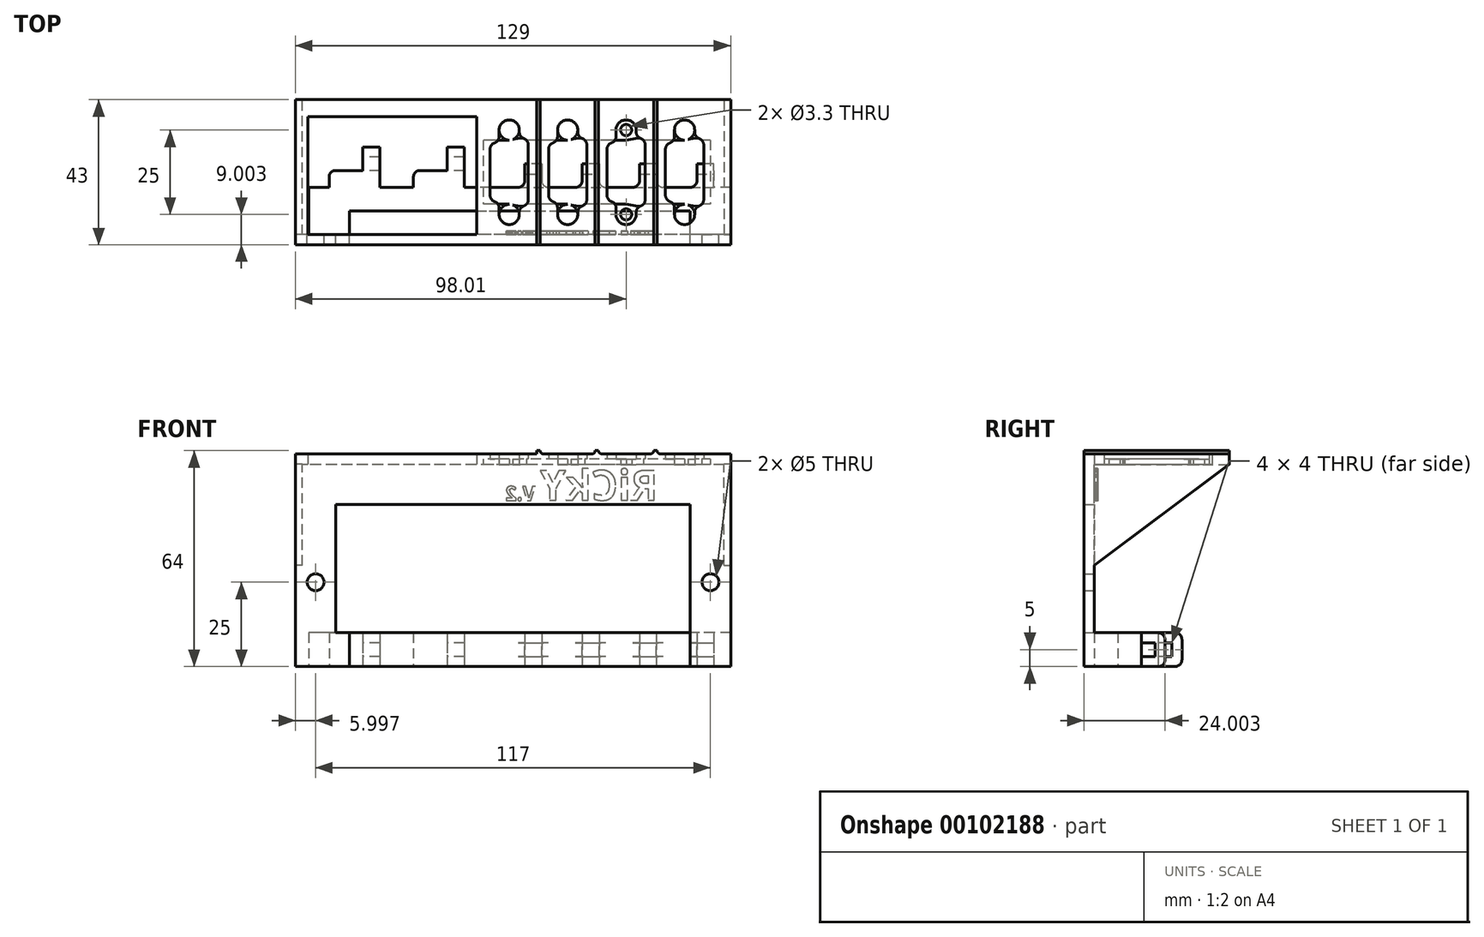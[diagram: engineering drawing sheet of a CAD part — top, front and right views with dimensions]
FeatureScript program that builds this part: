
annotation { "Feature Type Name" : "Feature", "Feature Type Description" : "" }
export const myFeature = defineFeature(function(context is Context, id is Id, definition is map)
    precondition{}
    {
        {
            var Q0;
            Q0=qCreatedBy(makeId("Top.planeOp"),FACE);
            var sketch = newSketch(context, id + "F0", { "sketchPlane" : qUnion([Q0])});
            skLineSegment(sketch, "E0", {"start": v(-4.26, 15.16) * mm, "end": v(16.74, 15.16) * mm});
            skLineSegment(sketch, "E1", {"start": v(-2.26, 3.83) * mm, "end": v(14.74, 3.83) * mm});
            skLineSegment(sketch, "E2", {"start": v(14.74, 3.83) * mm, "end": v(16.74, 15.16) * mm});
            skLineSegment(sketch, "E3", {"start": v(-2.26, 3.83) * mm, "end": v(-4.26, 15.16) * mm});
            skPoint(sketch, "E4", {"position": v(-3.26, 9.5) * mm});
            skPoint(sketch, "E5", {"position": v(15.74, 9.5) * mm});
            skPoint(sketch, "E6", {"position": v(-6.26, 9.5) * mm});
            skPoint(sketch, "E7", {"position": v(18.74, 9.5) * mm});
            skCircle(sketch, "E8", {"center": v(-6.26, 9.5) * mm, "radius": 3 * mm});
            skCircle(sketch, "E9", {"center": v(18.74, 9.5) * mm, "radius": 3 * mm});
            skLineSegment(sketch, "E10", {"start": v(-4.26, -2.17) * mm, "end": v(16.74, -2.17) * mm});
            skLineSegment(sketch, "E11", {"start": v(-2.26, -13.5) * mm, "end": v(14.74, -13.5) * mm});
            skLineSegment(sketch, "E12", {"start": v(14.74, -13.5) * mm, "end": v(16.74, -2.17) * mm});
            skLineSegment(sketch, "E13", {"start": v(-2.26, -13.5) * mm, "end": v(-4.26, -2.17) * mm});
            skPoint(sketch, "E14", {"position": v(-3.26, -7.83) * mm});
            skPoint(sketch, "E15", {"position": v(15.74, -7.83) * mm});
            skPoint(sketch, "E16", {"position": v(-6.26, -7.83) * mm});
            skPoint(sketch, "E17", {"position": v(18.74, -7.83) * mm});
            skCircle(sketch, "E18", {"center": v(-6.26, -7.83) * mm, "radius": 3 * mm});
            skCircle(sketch, "E19", {"center": v(18.74, -7.83) * mm, "radius": 3 * mm});
            skLineSegment(sketch, "E20", {"start": v(-4.26, 32.48) * mm, "end": v(16.74, 32.48) * mm});
            skLineSegment(sketch, "E21", {"start": v(-2.26, 21.16) * mm, "end": v(14.74, 21.16) * mm});
            skLineSegment(sketch, "E22", {"start": v(14.74, 21.16) * mm, "end": v(16.74, 32.48) * mm});
            skLineSegment(sketch, "E23", {"start": v(-2.26, 21.16) * mm, "end": v(-4.26, 32.48) * mm});
            skPoint(sketch, "E24", {"position": v(-3.26, 26.82) * mm});
            skPoint(sketch, "E25", {"position": v(15.74, 26.82) * mm});
            skPoint(sketch, "E26", {"position": v(-6.26, 26.82) * mm});
            skPoint(sketch, "E27", {"position": v(18.74, 26.82) * mm});
            skCircle(sketch, "E28", {"center": v(-6.26, 26.82) * mm, "radius": 3 * mm});
            skCircle(sketch, "E29", {"center": v(18.74, 26.82) * mm, "radius": 3 * mm});
            skLineSegment(sketch, "E30.bottom", {"start": v(27.74, 40.48) * mm, "end": v(-15.26, 40.48) * mm});
            skLineSegment(sketch, "E30.top", {"start": v(27.74, -88.52) * mm, "end": v(-15.26, -88.52) * mm});
            skLineSegment(sketch, "E30.left", {"start": v(27.74, 40.48) * mm, "end": v(27.74, -88.52) * mm});
            skLineSegment(sketch, "E30.right", {"start": v(-15.26, 40.48) * mm, "end": v(-15.26, -88.52) * mm});
            skLineSegment(sketch, "E31", {"start": v(-4.26, -19.5) * mm, "end": v(16.74, -19.5) * mm});
            skLineSegment(sketch, "E32", {"start": v(-2.26, -30.82) * mm, "end": v(14.74, -30.82) * mm});
            skLineSegment(sketch, "E33", {"start": v(14.74, -30.82) * mm, "end": v(16.74, -19.5) * mm});
            skLineSegment(sketch, "E34", {"start": v(-2.26, -30.82) * mm, "end": v(-4.26, -19.5) * mm});
            skPoint(sketch, "E35", {"position": v(-3.26, -25.15) * mm});
            skPoint(sketch, "E36", {"position": v(15.74, -25.15) * mm});
            skPoint(sketch, "E37", {"position": v(-6.26, -25.15) * mm});
            skPoint(sketch, "E38", {"position": v(18.74, -25.15) * mm});
            skCircle(sketch, "E39", {"center": v(-6.26, -25.15) * mm, "radius": 3 * mm});
            skCircle(sketch, "E40", {"center": v(18.74, -25.15) * mm, "radius": 3 * mm});
            skLineSegment(sketch, "E41", {"start": v(-6.26, 12.5) * mm, "end": v(-3.8, 12.5) * mm});
            skLineSegment(sketch, "E42", {"start": v(-6.26, 6.5) * mm, "end": v(-2.73, 6.5) * mm});
            skLineSegment(sketch, "E43", {"start": v(18.74, 12.5) * mm, "end": v(16.27, 12.5) * mm});
            skLineSegment(sketch, "E44", {"start": v(18.74, 6.5) * mm, "end": v(15.2, 6.5) * mm});
            skLineSegment(sketch, "E45", {"start": v(18.74, 29.82) * mm, "end": v(16.27, 29.82) * mm});
            skLineSegment(sketch, "E46", {"start": v(18.74, 23.82) * mm, "end": v(15.2, 23.82) * mm});
            skLineSegment(sketch, "E47", {"start": v(-6.26, 29.82) * mm, "end": v(-3.8, 29.82) * mm});
            skLineSegment(sketch, "E48", {"start": v(-6.26, 23.82) * mm, "end": v(-2.73, 23.82) * mm});
            skLineSegment(sketch, "E49", {"start": v(-6.26, -4.83) * mm, "end": v(-3.8, -4.83) * mm});
            skLineSegment(sketch, "E50", {"start": v(-6.26, -10.83) * mm, "end": v(-2.73, -10.83) * mm});
            skLineSegment(sketch, "E51", {"start": v(18.74, -10.83) * mm, "end": v(15.2, -10.83) * mm});
            skLineSegment(sketch, "E52", {"start": v(18.74, -4.83) * mm, "end": v(16.27, -4.83) * mm});
            skLineSegment(sketch, "E53", {"start": v(18.74, -22.15) * mm, "end": v(16.27, -22.15) * mm});
            skLineSegment(sketch, "E54", {"start": v(18.74, -28.15) * mm, "end": v(15.2, -28.15) * mm});
            skLineSegment(sketch, "E55", {"start": v(-6.26, -22.15) * mm, "end": v(-3.8, -22.15) * mm});
            skLineSegment(sketch, "E56", {"start": v(-6.26, -28.15) * mm, "end": v(-2.73, -28.15) * mm});
            skSolve(sketch);
        }
        {
            var Q0;
            Q0=makeQuery(id+"F0.imprint","IMPRINT",FACE,{"disambiguationData":[TD([[makeQuery(id+"F0.imprint","IMPRINT",EDGE,{"derivedFrom":sQuery(id+"F0.wireOp",EDGE,"E0")}),1.0]])]});
            extrude(context, id + "F1", {"entities" : qUnion([Q0]), "depth" : 3 * mm});
        }
        {
            var Q0;
            Q0=makeQuery(id+"F1.opExtrude","SWEPT_EDGE",EDGE,{"disambiguationData":[OSD([sQuery(id+"F0.wireOp",EDGE,"E0"),sQuery(id+"F0.wireOp",EDGE,"E3")])]});
            var Q1;
            Q1=makeQuery(id+"F1.opExtrude","SWEPT_EDGE",EDGE,{"disambiguationData":[OSD([sQuery(id+"F0.wireOp",EDGE,"E1"),sQuery(id+"F0.wireOp",EDGE,"E2")])]});
            var Q2;
            Q2=makeQuery(id+"F1.opExtrude","SWEPT_EDGE",EDGE,{"disambiguationData":[OSD([sQuery(id+"F0.wireOp",EDGE,"E0"),sQuery(id+"F0.wireOp",EDGE,"E2")])]});
            var Q3;
            Q3=makeQuery(id+"F1.opExtrude","SWEPT_EDGE",EDGE,{"disambiguationData":[OSD([sQuery(id+"F0.wireOp",EDGE,"E1"),sQuery(id+"F0.wireOp",EDGE,"E3")])]});
            var Q4;
            Q4=makeQuery(id+"F1.opExtrude","SWEPT_EDGE",EDGE,{"disambiguationData":[OSD([sQuery(id+"F0.wireOp",EDGE,"E20"),sQuery(id+"F0.wireOp",EDGE,"E23")])]});
            var Q5;
            Q5=makeQuery(id+"F1.opExtrude","SWEPT_EDGE",EDGE,{"disambiguationData":[OSD([sQuery(id+"F0.wireOp",EDGE,"E20"),sQuery(id+"F0.wireOp",EDGE,"E22")])]});
            var Q6;
            Q6=makeQuery(id+"F1.opExtrude","SWEPT_EDGE",EDGE,{"disambiguationData":[OSD([sQuery(id+"F0.wireOp",EDGE,"E21"),sQuery(id+"F0.wireOp",EDGE,"E23")])]});
            var Q7;
            Q7=makeQuery(id+"F1.opExtrude","SWEPT_EDGE",EDGE,{"disambiguationData":[OSD([sQuery(id+"F0.wireOp",EDGE,"E21"),sQuery(id+"F0.wireOp",EDGE,"E22")])]});
            var Q8;
            Q8=makeQuery(id+"F1.opExtrude","SWEPT_EDGE",EDGE,{"disambiguationData":[OSD([sQuery(id+"F0.wireOp",EDGE,"E11"),sQuery(id+"F0.wireOp",EDGE,"E12")])]});
            var Q9;
            Q9=makeQuery(id+"F1.opExtrude","SWEPT_EDGE",EDGE,{"disambiguationData":[OSD([sQuery(id+"F0.wireOp",EDGE,"E31"),sQuery(id+"F0.wireOp",EDGE,"E33")])]});
            var Q10;
            Q10=makeQuery(id+"F1.opExtrude","SWEPT_EDGE",EDGE,{"disambiguationData":[OSD([sQuery(id+"F0.wireOp",EDGE,"E10"),sQuery(id+"F0.wireOp",EDGE,"E12")])]});
            var Q11;
            Q11=makeQuery(id+"F1.opExtrude","SWEPT_EDGE",EDGE,{"disambiguationData":[OSD([sQuery(id+"F0.wireOp",EDGE,"E10"),sQuery(id+"F0.wireOp",EDGE,"E13")])]});
            var Q12;
            Q12=makeQuery(id+"F1.opExtrude","SWEPT_EDGE",EDGE,{"disambiguationData":[OSD([sQuery(id+"F0.wireOp",EDGE,"E31"),sQuery(id+"F0.wireOp",EDGE,"E34")])]});
            var Q13;
            Q13=makeQuery(id+"F1.opExtrude","SWEPT_EDGE",EDGE,{"disambiguationData":[OSD([sQuery(id+"F0.wireOp",EDGE,"E11"),sQuery(id+"F0.wireOp",EDGE,"E13")])]});
            var Q14;
            Q14=makeQuery(id+"F1.opExtrude","SWEPT_EDGE",EDGE,{"disambiguationData":[OSD([sQuery(id+"F0.wireOp",EDGE,"E32"),sQuery(id+"F0.wireOp",EDGE,"E34")])]});
            var Q15;
            Q15=makeQuery(id+"F1.opExtrude","SWEPT_EDGE",EDGE,{"disambiguationData":[OSD([sQuery(id+"F0.wireOp",EDGE,"E32"),sQuery(id+"F0.wireOp",EDGE,"E33")])]});
            fillet(context, id + "F2", {"entities" : qUnion([Q0, Q1, Q2, Q3, Q4, Q5, Q6, Q7, Q8, Q9, Q10, Q11, Q12, Q13, Q14, Q15]), "radius" : 2 * mm, "tangentPropagation" : true, "allowEdgeOverflow" : false});
        }
        {
            var Q0;
            Q0=makeQuery(id+"F0.imprint","IMPRINT",FACE,{"disambiguationData":[TD([[makeQuery(id+"F0.imprint","IMPRINT",EDGE,{"derivedFrom":sQuery(id+"F0.wireOp",EDGE,"E8")}),1.0]])]});
            var Q1;
            Q1=makeQuery(id+"F0.imprint","IMPRINT",FACE,{"disambiguationData":[TD([[makeQuery(id+"F0.imprint","IMPRINT",EDGE,{"derivedFrom":sQuery(id+"F0.wireOp",EDGE,"E9")}),1.0]])]});
            var Q2;
            {var subQ0=sQuery(id+"F0.wireOp",EDGE,"E28");var subQ1=sQuery(id+"F0.wireOp",EDGE,"E23");var subQ2=makeQuery(id+"F0.imprint","INTERSECT",VERTEX,{"disambiguationData":[OD(0.0)],"derivedFrom":[subQ1,subQ0]});Q2=makeQuery(id+"F0.imprint","IMPRINT",FACE,{"disambiguationData":[TD([[makeQuery(id+"F0.imprint","IMPRINT",EDGE,{"disambiguationData":[TD([[subQ2,-1.0]])],"derivedFrom":subQ1}),1.0]])]});}
            var Q3;
            {var subQ0=sQuery(id+"F0.wireOp",EDGE,"E29");var subQ1=sQuery(id+"F0.wireOp",EDGE,"E22");var subQ2=makeQuery(id+"F0.imprint","INTERSECT",VERTEX,{"disambiguationData":[OD(0.0)],"derivedFrom":[subQ1,subQ0]});Q3=makeQuery(id+"F0.imprint","IMPRINT",FACE,{"disambiguationData":[TD([[makeQuery(id+"F0.imprint","IMPRINT",EDGE,{"disambiguationData":[TD([[subQ2,-1.0]])],"derivedFrom":subQ1}),-1.0]])]});}
            var Q4;
            {var subQ0=sQuery(id+"F0.wireOp",EDGE,"E19");var subQ1=sQuery(id+"F0.wireOp",EDGE,"E12");var subQ2=makeQuery(id+"F0.imprint","INTERSECT",VERTEX,{"disambiguationData":[OD(0.0)],"derivedFrom":[subQ1,subQ0]});Q4=makeQuery(id+"F0.imprint","IMPRINT",FACE,{"disambiguationData":[TD([[makeQuery(id+"F0.imprint","IMPRINT",EDGE,{"disambiguationData":[TD([[subQ2,-1.0]])],"derivedFrom":subQ1}),-1.0]])]});}
            var Q5;
            {var subQ0=sQuery(id+"F0.wireOp",EDGE,"E18");var subQ1=sQuery(id+"F0.wireOp",EDGE,"E13");var subQ2=makeQuery(id+"F0.imprint","INTERSECT",VERTEX,{"disambiguationData":[OD(0.0)],"derivedFrom":[subQ1,subQ0]});Q5=makeQuery(id+"F0.imprint","IMPRINT",FACE,{"disambiguationData":[TD([[makeQuery(id+"F0.imprint","IMPRINT",EDGE,{"disambiguationData":[TD([[subQ2,-1.0]])],"derivedFrom":subQ1}),1.0]])]});}
            var Q6;
            {var subQ0=sQuery(id+"F0.wireOp",EDGE,"E40");var subQ1=sQuery(id+"F0.wireOp",EDGE,"E33");var subQ2=makeQuery(id+"F0.imprint","INTERSECT",VERTEX,{"disambiguationData":[OD(0.0)],"derivedFrom":[subQ1,subQ0]});Q6=makeQuery(id+"F0.imprint","IMPRINT",FACE,{"disambiguationData":[TD([[makeQuery(id+"F0.imprint","IMPRINT",EDGE,{"disambiguationData":[TD([[subQ2,-1.0]])],"derivedFrom":subQ1}),-1.0]])]});}
            var Q7;
            {var subQ0=sQuery(id+"F0.wireOp",EDGE,"E39");var subQ1=sQuery(id+"F0.wireOp",EDGE,"E34");var subQ2=makeQuery(id+"F0.imprint","INTERSECT",VERTEX,{"disambiguationData":[OD(0.0)],"derivedFrom":[subQ1,subQ0]});Q7=makeQuery(id+"F0.imprint","IMPRINT",FACE,{"disambiguationData":[TD([[makeQuery(id+"F0.imprint","IMPRINT",EDGE,{"disambiguationData":[TD([[subQ2,-1.0]])],"derivedFrom":subQ1}),1.0]])]});}
            var Q8;
            {var subQ0=sQuery(id+"F0.wireOp",EDGE,"E56");Q8=makeQuery(id+"F0.imprint","IMPRINT",FACE,{"disambiguationData":[TD([[makeQuery(id+"F0.imprint","IMPRINT",EDGE,{"derivedFrom":subQ0}),1.0]])]});}
            var Q9;
            {var subQ0=sQuery(id+"F0.wireOp",EDGE,"E55");Q9=makeQuery(id+"F0.imprint","IMPRINT",FACE,{"disambiguationData":[TD([[makeQuery(id+"F0.imprint","IMPRINT",EDGE,{"derivedFrom":subQ0}),-1.0]])]});}
            var Q10;
            {var subQ0=sQuery(id+"F0.wireOp",EDGE,"E54");Q10=makeQuery(id+"F0.imprint","IMPRINT",FACE,{"disambiguationData":[TD([[makeQuery(id+"F0.imprint","IMPRINT",EDGE,{"derivedFrom":subQ0}),-1.0]])]});}
            var Q11;
            {var subQ0=sQuery(id+"F0.wireOp",EDGE,"E53");Q11=makeQuery(id+"F0.imprint","IMPRINT",FACE,{"disambiguationData":[TD([[makeQuery(id+"F0.imprint","IMPRINT",EDGE,{"derivedFrom":subQ0}),1.0]])]});}
            var Q12;
            {var subQ0=sQuery(id+"F0.wireOp",EDGE,"E51");Q12=makeQuery(id+"F0.imprint","IMPRINT",FACE,{"disambiguationData":[TD([[makeQuery(id+"F0.imprint","IMPRINT",EDGE,{"derivedFrom":subQ0}),-1.0]])]});}
            var Q13;
            {var subQ0=sQuery(id+"F0.wireOp",EDGE,"E52");Q13=makeQuery(id+"F0.imprint","IMPRINT",FACE,{"disambiguationData":[TD([[makeQuery(id+"F0.imprint","IMPRINT",EDGE,{"derivedFrom":subQ0}),1.0]])]});}
            var Q14;
            {var subQ0=sQuery(id+"F0.wireOp",EDGE,"E50");Q14=makeQuery(id+"F0.imprint","IMPRINT",FACE,{"disambiguationData":[TD([[makeQuery(id+"F0.imprint","IMPRINT",EDGE,{"derivedFrom":subQ0}),1.0]])]});}
            var Q15;
            {var subQ0=sQuery(id+"F0.wireOp",EDGE,"E49");Q15=makeQuery(id+"F0.imprint","IMPRINT",FACE,{"disambiguationData":[TD([[makeQuery(id+"F0.imprint","IMPRINT",EDGE,{"derivedFrom":subQ0}),-1.0]])]});}
            var Q16;
            {var subQ0=sQuery(id+"F0.wireOp",EDGE,"E42");Q16=makeQuery(id+"F0.imprint","IMPRINT",FACE,{"disambiguationData":[TD([[makeQuery(id+"F0.imprint","IMPRINT",EDGE,{"derivedFrom":subQ0}),1.0]])]});}
            var Q17;
            {var subQ0=sQuery(id+"F0.wireOp",EDGE,"E41");Q17=makeQuery(id+"F0.imprint","IMPRINT",FACE,{"disambiguationData":[TD([[makeQuery(id+"F0.imprint","IMPRINT",EDGE,{"derivedFrom":subQ0}),-1.0]])]});}
            var Q18;
            {var subQ0=sQuery(id+"F0.wireOp",EDGE,"E44");Q18=makeQuery(id+"F0.imprint","IMPRINT",FACE,{"disambiguationData":[TD([[makeQuery(id+"F0.imprint","IMPRINT",EDGE,{"derivedFrom":subQ0}),-1.0]])]});}
            var Q19;
            {var subQ0=sQuery(id+"F0.wireOp",EDGE,"E43");Q19=makeQuery(id+"F0.imprint","IMPRINT",FACE,{"disambiguationData":[TD([[makeQuery(id+"F0.imprint","IMPRINT",EDGE,{"derivedFrom":subQ0}),1.0]])]});}
            var Q20;
            {var subQ0=sQuery(id+"F0.wireOp",EDGE,"E46");Q20=makeQuery(id+"F0.imprint","IMPRINT",FACE,{"disambiguationData":[TD([[makeQuery(id+"F0.imprint","IMPRINT",EDGE,{"derivedFrom":subQ0}),-1.0]])]});}
            var Q21;
            {var subQ0=sQuery(id+"F0.wireOp",EDGE,"E45");Q21=makeQuery(id+"F0.imprint","IMPRINT",FACE,{"disambiguationData":[TD([[makeQuery(id+"F0.imprint","IMPRINT",EDGE,{"derivedFrom":subQ0}),1.0]])]});}
            var Q22;
            {var subQ0=sQuery(id+"F0.wireOp",EDGE,"E47");Q22=makeQuery(id+"F0.imprint","IMPRINT",FACE,{"disambiguationData":[TD([[makeQuery(id+"F0.imprint","IMPRINT",EDGE,{"derivedFrom":subQ0}),-1.0]])]});}
            var Q23;
            {var subQ0=sQuery(id+"F0.wireOp",EDGE,"E48");Q23=makeQuery(id+"F0.imprint","IMPRINT",FACE,{"disambiguationData":[TD([[makeQuery(id+"F0.imprint","IMPRINT",EDGE,{"derivedFrom":subQ0}),1.0]])]});}
            extrude(context, id + "F3", {"entities" : qUnion([Q0, Q1, Q2, Q3, Q4, Q5, Q6, Q7, Q8, Q9, Q10, Q11, Q12, Q13, Q14, Q15, Q16, Q17, Q18, Q19, Q20, Q21, Q22, Q23]), "operationType" : NewBodyOperationType.ADD, "depth" : 1.5 * mm});
        }
        {
            var Q0;
            Q0=sQuery(id+"F0.wireOp",VERTEX,"E6");
            var Q1;
            Q1=sQuery(id+"F0.wireOp",VERTEX,"E7");
            var Q2;
            Q2=sQuery(id+"F0.wireOp",VERTEX,"E26");
            var Q3;
            Q3=sQuery(id+"F0.wireOp",VERTEX,"E27");
            var Q4;
            Q4=sQuery(id+"F0.wireOp",VERTEX,"E17");
            var Q5;
            Q5=sQuery(id+"F0.wireOp",VERTEX,"E16");
            var Q6;
            Q6=sQuery(id+"F0.wireOp",VERTEX,"E38");
            var Q7;
            Q7=sQuery(id+"F0.wireOp",VERTEX,"E37");
            var Q8;
            Q8=makeQuery(id+"F1.opExtrude","SWEPT_BODY",BODY,{"disambiguationData":[OSD([sQuery(id+"F0.wireOp",EDGE,"E0"),sQuery(id+"F0.wireOp",EDGE,"E1"),sQuery(id+"F0.wireOp",EDGE,"E2"),sQuery(id+"F0.wireOp",EDGE,"E3"),sQuery(id+"F0.wireOp",EDGE,"Wovf68Om-m2Ft-W6fg-vgO9-NATX11qrs2Ft.bottom"),sQuery(id+"F0.wireOp",EDGE,"Wovf68Om-m2Ft-W6fg-vgO9-NATX11qrs2Ft.top"),sQuery(id+"F0.wireOp",EDGE,"Wovf68Om-m2Ft-W6fg-vgO9-NATX11qrs2Ft.left"),sQuery(id+"F0.wireOp",EDGE,"Wovf68Om-m2Ft-W6fg-vgO9-NATX11qrs2Ft.right")])]});
            hole(context, id + "F4", {"style" : HoleStyle.SIMPLE, "endStyle" : HoleEndStyle.THROUGH, "oppositeDirection" : true, "holeDiameter" : 3.3 * mm, "startFromSketch" : true, "locations" : qUnion([Q0, Q1, Q2, Q3, Q4, Q5, Q6, Q7]), "scope" : qUnion([Q8]), "isTappedThrough" : true});
        }
        {
            var Q0;
            {var subQ0=sQuery(id+"F0.wireOp",EDGE,"E39");var subQ1=sQuery(id+"F0.wireOp",EDGE,"E34");var subQ2=sQuery(id+"F0.wireOp",EDGE,"E40");var subQ3=sQuery(id+"F0.wireOp",EDGE,"E33");var subQ4=sQuery(id+"F0.wireOp",EDGE,"E28");var subQ5=sQuery(id+"F0.wireOp",EDGE,"E23");var subQ6=sQuery(id+"F0.wireOp",EDGE,"E29");var subQ7=sQuery(id+"F0.wireOp",EDGE,"E22");var subQ8=sQuery(id+"F0.wireOp",EDGE,"E18");var subQ9=sQuery(id+"F0.wireOp",EDGE,"E13");var subQ10=sQuery(id+"F0.wireOp",EDGE,"E19");var subQ11=sQuery(id+"F0.wireOp",EDGE,"E12");var subQ12=sQuery(id+"F0.wireOp",EDGE,"E9");var subQ13=sQuery(id+"F0.wireOp",EDGE,"E8");Q0=makeQuery(id+"F3.boolean.opBoolean","MERGE",FACE,{"derivedFrom":[makeQuery(id+"F1.opExtrude","CAP_FACE",FACE,{"disambiguationData":[OSD([sQuery(id+"F0.wireOp",EDGE,"E0"),sQuery(id+"F0.wireOp",EDGE,"E1"),sQuery(id+"F0.wireOp",EDGE,"E2"),sQuery(id+"F0.wireOp",EDGE,"E3"),subQ13,subQ12,sQuery(id+"F0.wireOp",EDGE,"E10"),sQuery(id+"F0.wireOp",EDGE,"E11"),subQ11,subQ9,subQ8,subQ10,sQuery(id+"F0.wireOp",EDGE,"E20"),sQuery(id+"F0.wireOp",EDGE,"E21"),subQ7,subQ5,subQ4,subQ6,sQuery(id+"F0.wireOp",EDGE,"E30.bottom"),sQuery(id+"F0.wireOp",EDGE,"E30.top"),sQuery(id+"F0.wireOp",EDGE,"E30.left"),sQuery(id+"F0.wireOp",EDGE,"E30.right"),sQuery(id+"F0.wireOp",EDGE,"E31"),sQuery(id+"F0.wireOp",EDGE,"E32"),subQ3,subQ1,subQ0,subQ2])],"isStart":true}),makeQuery(id+"F3.opExtrude","CAP_FACE",FACE,{"disambiguationData":[OSD([subQ13])],"isStart":true}),makeQuery(id+"F3.opExtrude","CAP_FACE",FACE,{"disambiguationData":[OSD([subQ12])],"isStart":true}),makeQuery(id+"F3.opExtrude","CAP_FACE",FACE,{"disambiguationData":[OSD([subQ11,subQ10])],"isStart":true}),makeQuery(id+"F3.opExtrude","CAP_FACE",FACE,{"disambiguationData":[OSD([subQ9,subQ8])],"isStart":true}),makeQuery(id+"F3.opExtrude","CAP_FACE",FACE,{"disambiguationData":[OSD([subQ7,subQ6])],"isStart":true}),makeQuery(id+"F3.opExtrude","CAP_FACE",FACE,{"disambiguationData":[OSD([subQ5,subQ4])],"isStart":true}),makeQuery(id+"F3.opExtrude","CAP_FACE",FACE,{"disambiguationData":[OSD([subQ3,subQ2])],"isStart":true}),makeQuery(id+"F3.opExtrude","CAP_FACE",FACE,{"disambiguationData":[OSD([subQ1,subQ0])],"isStart":true})]});}
            var sketch = newSketch(context, id + "F5", { "sketchPlane" : qUnion([Q0])});
            skLineSegment(sketch, "E57.bottom", {"start": v(24.74, -40.48) * mm, "end": v(27.74, -40.48) * mm});
            skLineSegment(sketch, "E57.top", {"start": v(24.74, 88.52) * mm, "end": v(27.74, 88.52) * mm});
            skLineSegment(sketch, "E57.left", {"start": v(24.74, -40.48) * mm, "end": v(24.74, 88.52) * mm});
            skLineSegment(sketch, "E57.right", {"start": v(27.74, -40.48) * mm, "end": v(27.74, 88.52) * mm});
            skSolve(sketch);
        }
        {
            var Q0;
            Q0=makeQuery(id+"F5.imprint","IMPRINT",FACE,{"disambiguationData":[TD([[makeQuery(id+"F5.imprint","IMPRINT",EDGE,{"derivedFrom":sQuery(id+"F5.wireOp",EDGE,"E57.bottom")}),-1.0]])]});
            extrude(context, id + "F6", {"entities" : qUnion([Q0]), "operationType" : NewBodyOperationType.ADD, "depth" : 60 * mm});
        }
        {
            var Q0;
            Q0=makeQuery(id+"F6.boolean.opBoolean","MERGE",FACE,{"derivedFrom":[makeQuery(id+"F1.opExtrude","SWEPT_FACE",FACE,{"disambiguationData":[OSD([sQuery(id+"F0.wireOp",EDGE,"E30.bottom")])]}),makeQuery(id+"F6.opExtrude","SWEPT_FACE",FACE,{"disambiguationData":[OSD([sQuery(id+"F5.wireOp",EDGE,"E57.bottom")])]})]});
            var sketch = newSketch(context, id + "F7", { "sketchPlane" : qUnion([Q0])});
            skLineSegment(sketch, "E58", {"start": v(15.26, 0) * mm, "end": v(-24.74, -30) * mm});
            skLineSegment(sketch, "E59", {"start": v(-24.74, -30) * mm, "end": v(-24.74, 0) * mm});
            skLineSegment(sketch, "E60", {"start": v(-24.74, 0) * mm, "end": v(15.26, 0) * mm});
            skSolve(sketch);
        }
        {
            var Q0;
            Q0=makeQuery(id+"F6.boolean.opBoolean","MERGE",FACE,{"derivedFrom":[makeQuery(id+"F1.opExtrude","SWEPT_FACE",FACE,{"disambiguationData":[OSD([sQuery(id+"F0.wireOp",EDGE,"E30.top")])]}),makeQuery(id+"F6.opExtrude","SWEPT_FACE",FACE,{"disambiguationData":[OSD([sQuery(id+"F5.wireOp",EDGE,"E57.top")])]})]});
            var sketch = newSketch(context, id + "F8", { "sketchPlane" : qUnion([Q0])});
            skLineSegment(sketch, "E61", {"start": v(-15.26, 0) * mm, "end": v(24.74, -30) * mm});
            skSolve(sketch);
        }
        {
            var Q0;
            Q0=makeQuery(id+"F7.imprint","IMPRINT",FACE,{"disambiguationData":[TD([[makeQuery(id+"F7.imprint","IMPRINT",EDGE,{"derivedFrom":sQuery(id+"F7.wireOp",EDGE,"E58")}),-1.0]])]});
            extrude(context, id + "F9", {"entities" : qUnion([Q0]), "operationType" : NewBodyOperationType.ADD, "oppositeDirection" : true, "depth" : 2 * mm});
        }
        {
            var Q0;
            {var subQ0=sQuery(id+"F8.wireOp",EDGE,"E61");Q0=makeQuery(id+"F8.imprint","IMPRINT",FACE,{"disambiguationData":[TD([[makeQuery(id+"F8.imprint","IMPRINT",EDGE,{"derivedFrom":subQ0}),1.0]])]});}
            extrude(context, id + "F10", {"entities" : qUnion([Q0]), "operationType" : NewBodyOperationType.ADD, "oppositeDirection" : true, "depth" : 2 * mm});
        }
        {
            var Q0;
            Q0=makeQuery(id+"F6.opExtrude","SWEPT_FACE",FACE,{"disambiguationData":[OSD([sQuery(id+"F5.wireOp",EDGE,"E57.left")])]});
            var sketch = newSketch(context, id + "F11", { "sketchPlane" : qUnion([Q0])});
            skLineSegment(sketch, "E62.bottom", {"start": v(-28.48, -12) * mm, "end": v(76.52, -12) * mm});
            skLineSegment(sketch, "E62.top", {"start": v(-28.48, -52) * mm, "end": v(76.52, -52) * mm});
            skLineSegment(sketch, "E62.left", {"start": v(-28.48, -12) * mm, "end": v(-28.48, -52) * mm});
            skLineSegment(sketch, "E62.right", {"start": v(76.52, -12) * mm, "end": v(76.52, -52) * mm});
            skPoint(sketch, "E63.positionSnap0", {"position": v(24.02, 0) * mm});
            skSolve(sketch);
        }
        {
            var Q0;
            Q0=makeQuery(id+"F11.imprint","IMPRINT",FACE,{"disambiguationData":[TD([[makeQuery(id+"F11.imprint","IMPRINT",EDGE,{"derivedFrom":sQuery(id+"F11.wireOp",EDGE,"E62.bottom")}),-1.0]])]});
            extrude(context, id + "F12", {"entities" : qUnion([Q0]), "operationType" : NewBodyOperationType.REMOVE, "oppositeDirection" : true, "depth" : 3 * mm});
        }
        {
            var Q0;
            Q0=makeQuery(id+"F1.opExtrude","SWEPT_EDGE",EDGE,{"disambiguationData":[OSD([sQuery(id+"F0.wireOp",EDGE,"E34"),sQuery(id+"F0.wireOp",EDGE,"E56")])]});
            var Q1;
            Q1=makeQuery(id+"F1.opExtrude","SWEPT_EDGE",EDGE,{"disambiguationData":[OSD([sQuery(id+"F0.wireOp",EDGE,"E34"),sQuery(id+"F0.wireOp",EDGE,"E55")])]});
            var Q2;
            Q2=makeQuery(id+"F1.opExtrude","SWEPT_EDGE",EDGE,{"disambiguationData":[OSD([sQuery(id+"F0.wireOp",EDGE,"E33"),sQuery(id+"F0.wireOp",EDGE,"E54")])]});
            var Q3;
            Q3=makeQuery(id+"F1.opExtrude","SWEPT_EDGE",EDGE,{"disambiguationData":[OSD([sQuery(id+"F0.wireOp",EDGE,"E33"),sQuery(id+"F0.wireOp",EDGE,"E53")])]});
            var Q4;
            Q4=makeQuery(id+"F1.opExtrude","SWEPT_EDGE",EDGE,{"disambiguationData":[OSD([sQuery(id+"F0.wireOp",EDGE,"E12"),sQuery(id+"F0.wireOp",EDGE,"E52")])]});
            var Q5;
            Q5=makeQuery(id+"F1.opExtrude","SWEPT_EDGE",EDGE,{"disambiguationData":[OSD([sQuery(id+"F0.wireOp",EDGE,"E13"),sQuery(id+"F0.wireOp",EDGE,"E49")])]});
            var Q6;
            Q6=makeQuery(id+"F1.opExtrude","SWEPT_EDGE",EDGE,{"disambiguationData":[OSD([sQuery(id+"F0.wireOp",EDGE,"E13"),sQuery(id+"F0.wireOp",EDGE,"E50")])]});
            var Q7;
            Q7=makeQuery(id+"F1.opExtrude","SWEPT_EDGE",EDGE,{"disambiguationData":[OSD([sQuery(id+"F0.wireOp",EDGE,"E12"),sQuery(id+"F0.wireOp",EDGE,"E51")])]});
            var Q8;
            Q8=makeQuery(id+"F1.opExtrude","SWEPT_EDGE",EDGE,{"disambiguationData":[OSD([sQuery(id+"F0.wireOp",EDGE,"E3"),sQuery(id+"F0.wireOp",EDGE,"E42")])]});
            var Q9;
            Q9=makeQuery(id+"F1.opExtrude","SWEPT_EDGE",EDGE,{"disambiguationData":[OSD([sQuery(id+"F0.wireOp",EDGE,"E2"),sQuery(id+"F0.wireOp",EDGE,"E44")])]});
            var Q10;
            Q10=makeQuery(id+"F1.opExtrude","SWEPT_EDGE",EDGE,{"disambiguationData":[OSD([sQuery(id+"F0.wireOp",EDGE,"E22"),sQuery(id+"F0.wireOp",EDGE,"E46")])]});
            var Q11;
            Q11=makeQuery(id+"F1.opExtrude","SWEPT_EDGE",EDGE,{"disambiguationData":[OSD([sQuery(id+"F0.wireOp",EDGE,"E23"),sQuery(id+"F0.wireOp",EDGE,"E48")])]});
            var Q12;
            Q12=makeQuery(id+"F1.opExtrude","SWEPT_EDGE",EDGE,{"disambiguationData":[OSD([sQuery(id+"F0.wireOp",EDGE,"E3"),sQuery(id+"F0.wireOp",EDGE,"E41")])]});
            var Q13;
            Q13=makeQuery(id+"F1.opExtrude","SWEPT_EDGE",EDGE,{"disambiguationData":[OSD([sQuery(id+"F0.wireOp",EDGE,"E2"),sQuery(id+"F0.wireOp",EDGE,"E43")])]});
            var Q14;
            Q14=makeQuery(id+"F1.opExtrude","SWEPT_EDGE",EDGE,{"disambiguationData":[OSD([sQuery(id+"F0.wireOp",EDGE,"E22"),sQuery(id+"F0.wireOp",EDGE,"E45")])]});
            var Q15;
            Q15=makeQuery(id+"F1.opExtrude","SWEPT_EDGE",EDGE,{"disambiguationData":[OSD([sQuery(id+"F0.wireOp",EDGE,"E23"),sQuery(id+"F0.wireOp",EDGE,"E47")])]});
            fillet(context, id + "F13", {"entities" : qUnion([Q0, Q1, Q2, Q3, Q4, Q5, Q6, Q7, Q8, Q9, Q10, Q11, Q12, Q13, Q14, Q15]), "radius" : 2 * mm, "tangentPropagation" : true, "allowEdgeOverflow" : false});
        }
        {
            var Q0;
            Q0=makeQuery(id+"F1.opExtrude","SWEPT_BODY",BODY,{"disambiguationData":[OSD([sQuery(id+"F0.wireOp",EDGE,"E0"),sQuery(id+"F0.wireOp",EDGE,"E1"),sQuery(id+"F0.wireOp",EDGE,"E2"),sQuery(id+"F0.wireOp",EDGE,"E3"),sQuery(id+"F0.wireOp",EDGE,"E8"),sQuery(id+"F0.wireOp",EDGE,"E9"),sQuery(id+"F0.wireOp",EDGE,"E10"),sQuery(id+"F0.wireOp",EDGE,"E11"),sQuery(id+"F0.wireOp",EDGE,"E12"),sQuery(id+"F0.wireOp",EDGE,"E13"),sQuery(id+"F0.wireOp",EDGE,"E18"),sQuery(id+"F0.wireOp",EDGE,"E19"),sQuery(id+"F0.wireOp",EDGE,"E20"),sQuery(id+"F0.wireOp",EDGE,"E21"),sQuery(id+"F0.wireOp",EDGE,"E22"),sQuery(id+"F0.wireOp",EDGE,"E23"),sQuery(id+"F0.wireOp",EDGE,"E28"),sQuery(id+"F0.wireOp",EDGE,"E29"),sQuery(id+"F0.wireOp",EDGE,"E30.bottom"),sQuery(id+"F0.wireOp",EDGE,"E30.top"),sQuery(id+"F0.wireOp",EDGE,"E30.left"),sQuery(id+"F0.wireOp",EDGE,"E30.right"),sQuery(id+"F0.wireOp",EDGE,"E31"),sQuery(id+"F0.wireOp",EDGE,"E32"),sQuery(id+"F0.wireOp",EDGE,"E33"),sQuery(id+"F0.wireOp",EDGE,"E34"),sQuery(id+"F0.wireOp",EDGE,"E39"),sQuery(id+"F0.wireOp",EDGE,"E40"),sQuery(id+"F0.wireOp",EDGE,"E41"),sQuery(id+"F0.wireOp",EDGE,"E42"),sQuery(id+"F0.wireOp",EDGE,"E43"),sQuery(id+"F0.wireOp",EDGE,"E44"),sQuery(id+"F0.wireOp",EDGE,"E45"),sQuery(id+"F0.wireOp",EDGE,"E46"),sQuery(id+"F0.wireOp",EDGE,"E47"),sQuery(id+"F0.wireOp",EDGE,"E48"),sQuery(id+"F0.wireOp",EDGE,"E49"),sQuery(id+"F0.wireOp",EDGE,"E50"),sQuery(id+"F0.wireOp",EDGE,"E51"),sQuery(id+"F0.wireOp",EDGE,"E52"),sQuery(id+"F0.wireOp",EDGE,"E53"),sQuery(id+"F0.wireOp",EDGE,"E54"),sQuery(id+"F0.wireOp",EDGE,"E55"),sQuery(id+"F0.wireOp",EDGE,"E56")])]});
            var Q1;
            Q1=makeQuery(id+"F6.boolean.opBoolean","MERGE",EDGE,{"derivedFrom":[makeQuery(id+"F1.opExtrude","SWEPT_EDGE",EDGE,{"disambiguationData":[OSD([sQuery(id+"F0.wireOp",EDGE,"E30.top"),sQuery(id+"F0.wireOp",EDGE,"E30.left")])]}),makeQuery(id+"F6.opExtrude","SWEPT_EDGE",EDGE,{"disambiguationData":[OSD([sQuery(id+"F5.wireOp",EDGE,"E57.top"),sQuery(id+"F5.wireOp",EDGE,"E57.right")])]})]});
            transform(context, id + "F14", {"entities" : qUnion([Q0]), "transformType" : TransformType.ROTATION, "transformAxis" : qUnion([Q1]), "angle" : 90 * degree, "makeCopy" : false});
        }
        {
            var Q0;
            {var subQ0=sQuery(id+"F8EoDyI46MSBQYM_1.wireOp",EDGE,"hDJBzksL-QToe-umQY-51Cy-cnB0OUttW4tD.bottom");var subQ1=sQuery(id+"F8EoDyI46MSBQYM_1.wireOp",EDGE,"pdXBlQge-3E0r-zufv-tM46-rPFQcP1RDKDh.bottom");var subQ2=sQuery(id+"F0.wireOp",EDGE,"E56");var subQ3=sQuery(id+"F0.wireOp",EDGE,"E55");var subQ4=sQuery(id+"F0.wireOp",EDGE,"E39");var subQ5=sQuery(id+"F0.wireOp",EDGE,"E34");var subQ6=sQuery(id+"F0.wireOp",EDGE,"E54");var subQ7=sQuery(id+"F0.wireOp",EDGE,"E53");var subQ8=sQuery(id+"F0.wireOp",EDGE,"E40");var subQ9=sQuery(id+"F0.wireOp",EDGE,"E33");var subQ10=sQuery(id+"F0.wireOp",EDGE,"E48");var subQ11=sQuery(id+"F0.wireOp",EDGE,"E47");var subQ12=sQuery(id+"F0.wireOp",EDGE,"E28");var subQ13=sQuery(id+"F0.wireOp",EDGE,"E23");var subQ14=sQuery(id+"F0.wireOp",EDGE,"E46");var subQ15=sQuery(id+"F0.wireOp",EDGE,"E45");var subQ16=sQuery(id+"F0.wireOp",EDGE,"E29");var subQ17=sQuery(id+"F0.wireOp",EDGE,"E22");var subQ18=sQuery(id+"F0.wireOp",EDGE,"E50");var subQ19=sQuery(id+"F0.wireOp",EDGE,"E49");var subQ20=sQuery(id+"F0.wireOp",EDGE,"E18");var subQ21=sQuery(id+"F0.wireOp",EDGE,"E13");var subQ22=sQuery(id+"F0.wireOp",EDGE,"E52");var subQ23=sQuery(id+"F0.wireOp",EDGE,"E51");var subQ24=sQuery(id+"F0.wireOp",EDGE,"E19");var subQ25=sQuery(id+"F0.wireOp",EDGE,"E12");var subQ26=sQuery(id+"F0.wireOp",EDGE,"E42");var subQ27=sQuery(id+"F0.wireOp",EDGE,"E41");var subQ28=sQuery(id+"F0.wireOp",EDGE,"E8");var subQ29=sQuery(id+"F0.wireOp",EDGE,"E3");var subQ30=sQuery(id+"F0.wireOp",EDGE,"E44");var subQ31=sQuery(id+"F0.wireOp",EDGE,"E43");var subQ32=sQuery(id+"F0.wireOp",EDGE,"E9");var subQ33=sQuery(id+"F0.wireOp",EDGE,"E2");Q0=makeQuery(id+"FhEWOf1GAh2BQzi_1.boolean.opBoolean","MERGE",FACE,{"derivedFrom":[makeQuery(id+"FwzRGj0mSM9Jiqs_1.boolean.opBoolean","MERGE",FACE,{"derivedFrom":[makeQuery(id+"F3.boolean.opBoolean","MERGE",FACE,{"derivedFrom":[makeQuery(id+"F1.opExtrude","CAP_FACE",FACE,{"disambiguationData":[OSD([sQuery(id+"F0.wireOp",EDGE,"E0"),sQuery(id+"F0.wireOp",EDGE,"E1"),subQ33,subQ29,subQ28,subQ32,sQuery(id+"F0.wireOp",EDGE,"E10"),sQuery(id+"F0.wireOp",EDGE,"E11"),subQ25,subQ21,subQ20,subQ24,sQuery(id+"F0.wireOp",EDGE,"E20"),sQuery(id+"F0.wireOp",EDGE,"E21"),subQ17,subQ13,subQ12,subQ16,sQuery(id+"F0.wireOp",EDGE,"E30.bottom"),sQuery(id+"F0.wireOp",EDGE,"E30.top"),sQuery(id+"F0.wireOp",EDGE,"E30.left"),sQuery(id+"F0.wireOp",EDGE,"E30.right"),sQuery(id+"F0.wireOp",EDGE,"E31"),sQuery(id+"F0.wireOp",EDGE,"E32"),subQ9,subQ5,subQ4,subQ8,subQ27,subQ26,subQ31,subQ30,subQ15,subQ14,subQ11,subQ10,subQ19,subQ18,subQ23,subQ22,subQ7,subQ6,subQ3,subQ2])],"isStart":true}),makeQuery(id+"F3.opExtrude","CAP_FACE",FACE,{"disambiguationData":[OSD([subQ33,subQ32,subQ31,subQ30])],"isStart":true}),makeQuery(id+"F3.opExtrude","CAP_FACE",FACE,{"disambiguationData":[OSD([subQ29,subQ28,subQ27,subQ26])],"isStart":true}),makeQuery(id+"F3.opExtrude","CAP_FACE",FACE,{"disambiguationData":[OSD([subQ25,subQ24,subQ23,subQ22])],"isStart":true}),makeQuery(id+"F3.opExtrude","CAP_FACE",FACE,{"disambiguationData":[OSD([subQ21,subQ20,subQ19,subQ18])],"isStart":true}),makeQuery(id+"F3.opExtrude","CAP_FACE",FACE,{"disambiguationData":[OSD([subQ17,subQ16,subQ15,subQ14])],"isStart":true}),makeQuery(id+"F3.opExtrude","CAP_FACE",FACE,{"disambiguationData":[OSD([subQ13,subQ12,subQ11,subQ10])],"isStart":true}),makeQuery(id+"F3.opExtrude","CAP_FACE",FACE,{"disambiguationData":[OSD([subQ9,subQ8,subQ7,subQ6])],"isStart":true}),makeQuery(id+"F3.opExtrude","CAP_FACE",FACE,{"disambiguationData":[OSD([subQ5,subQ4,subQ3,subQ2])],"isStart":true})]}),makeQuery(id+"FwzRGj0mSM9Jiqs_1.opExtrude","SWEPT_FACE",FACE,{"disambiguationData":[OSD([subQ1])]}),makeQuery(id+"FwzRGj0mSM9Jiqs_1.opExtrude","SWEPT_FACE",FACE,{"disambiguationData":[OSD([subQ0])]})]}),makeQuery(id+"FhEWOf1GAh2BQzi_1.opExtrude","SWEPT_FACE",FACE,{"disambiguationData":[OSD([subQ1])]}),makeQuery(id+"FhEWOf1GAh2BQzi_1.opExtrude","SWEPT_FACE",FACE,{"disambiguationData":[OSD([subQ0])]})]});}
            var sketch = newSketch(context, id + "F15", { "sketchPlane" : qUnion([Q0])});
            skLineSegment(sketch, "E64.bottom", {"start": v(150.74, 57.52) * mm, "end": v(83.44, 57.52) * mm});
            skLineSegment(sketch, "E64.top", {"start": v(150.74, 76.52) * mm, "end": v(83.44, 76.52) * mm});
            skLineSegment(sketch, "E64.left", {"start": v(150.74, 57.52) * mm, "end": v(150.74, 76.52) * mm});
            skLineSegment(sketch, "E64.right", {"start": v(83.44, 57.52) * mm, "end": v(83.44, 76.52) * mm});
            skSolve(sketch);
        }
        {
            var Q0;
            {var subQ10=sQuery(id+"F0.wireOp",EDGE,"E0");var subQ24=makeQuery(id+"F1.opExtrude","CAP_EDGE",EDGE,{"disambiguationData":[OSD([subQ10])],"isStart":true});Q0=makeQuery(id+"F15.imprint","IMPRINT",FACE,{"disambiguationData":[TD([[makeQuery(id+"F15.imprint","IMPRINT",EDGE,{"derivedFrom":subQ24}),-1.0]])]});}
            var Q1;
            {var subQ0=sQuery(id+"F15.wireOp",EDGE,"E64.left");Q1=makeQuery(id+"F15.imprint","IMPRINT",FACE,{"disambiguationData":[TD([[makeQuery(id+"F15.imprint","IMPRINT",EDGE,{"derivedFrom":subQ0}),1.0]])]});}
            var Q2;
            {var subQ9=sQuery(id+"F0.wireOp",EDGE,"E1");Q2=makeQuery(id+"F15.imprint","IMPRINT",FACE,{"disambiguationData":[TD([[makeQuery(id+"F15.imprint","IMPRINT",EDGE,{"derivedFrom":makeQuery(id+"F1.opExtrude","CAP_EDGE",EDGE,{"disambiguationData":[OSD([subQ9])],"isStart":true})}),1.0]])]});}
            var Q3;
            {var subQ9=sQuery(id+"F0.wireOp",EDGE,"E11");Q3=makeQuery(id+"F15.imprint","IMPRINT",FACE,{"disambiguationData":[TD([[makeQuery(id+"F15.imprint","IMPRINT",EDGE,{"derivedFrom":makeQuery(id+"F1.opExtrude","CAP_EDGE",EDGE,{"disambiguationData":[OSD([subQ9])],"isStart":true})}),1.0]])]});}
            var Q4;
            {var subQ10=sQuery(id+"F15.wireOp",EDGE,"E64.right");Q4=makeQuery(id+"F15.imprint","IMPRINT",FACE,{"disambiguationData":[TD([[makeQuery(id+"F15.imprint","IMPRINT",EDGE,{"derivedFrom":subQ10}),-1.0]])]});}
            extrude(context, id + "F16", {"entities" : qUnion([Q0, Q1, Q2, Q3, Q4]), "operationType" : NewBodyOperationType.REMOVE, "oppositeDirection" : true, "depth" : 1.5 * mm});
        }
        {
            var Q0;
            {var subQ0=sQuery(id+"F0.wireOp",EDGE,"E56");var subQ1=sQuery(id+"F0.wireOp",EDGE,"E55");var subQ2=sQuery(id+"F0.wireOp",EDGE,"E39");var subQ3=sQuery(id+"F0.wireOp",EDGE,"E34");var subQ4=sQuery(id+"F0.wireOp",EDGE,"E54");var subQ5=sQuery(id+"F0.wireOp",EDGE,"E53");var subQ6=sQuery(id+"F0.wireOp",EDGE,"E40");var subQ7=sQuery(id+"F0.wireOp",EDGE,"E33");var subQ8=sQuery(id+"F0.wireOp",EDGE,"E48");var subQ9=sQuery(id+"F0.wireOp",EDGE,"E47");var subQ10=sQuery(id+"F0.wireOp",EDGE,"E28");var subQ11=sQuery(id+"F0.wireOp",EDGE,"E23");var subQ12=sQuery(id+"F0.wireOp",EDGE,"E46");var subQ13=sQuery(id+"F0.wireOp",EDGE,"E45");var subQ14=sQuery(id+"F0.wireOp",EDGE,"E29");var subQ15=sQuery(id+"F0.wireOp",EDGE,"E22");var subQ16=sQuery(id+"F0.wireOp",EDGE,"E50");var subQ17=sQuery(id+"F0.wireOp",EDGE,"E49");var subQ18=sQuery(id+"F0.wireOp",EDGE,"E18");var subQ19=sQuery(id+"F0.wireOp",EDGE,"E13");var subQ20=sQuery(id+"F0.wireOp",EDGE,"E52");var subQ21=sQuery(id+"F0.wireOp",EDGE,"E51");var subQ22=sQuery(id+"F0.wireOp",EDGE,"E19");var subQ23=sQuery(id+"F0.wireOp",EDGE,"E12");var subQ24=sQuery(id+"F0.wireOp",EDGE,"E42");var subQ25=sQuery(id+"F0.wireOp",EDGE,"E41");var subQ26=sQuery(id+"F0.wireOp",EDGE,"E8");var subQ27=sQuery(id+"F0.wireOp",EDGE,"E3");var subQ28=sQuery(id+"F0.wireOp",EDGE,"E44");var subQ29=sQuery(id+"F0.wireOp",EDGE,"E43");var subQ30=sQuery(id+"F0.wireOp",EDGE,"E9");var subQ31=sQuery(id+"F0.wireOp",EDGE,"E2");Q0=makeQuery(id+"F3.boolean.opBoolean","MERGE",FACE,{"derivedFrom":[makeQuery(id+"F1.opExtrude","CAP_FACE",FACE,{"disambiguationData":[OSD([sQuery(id+"F0.wireOp",EDGE,"E0"),sQuery(id+"F0.wireOp",EDGE,"E1"),subQ31,subQ27,subQ26,subQ30,sQuery(id+"F0.wireOp",EDGE,"E10"),sQuery(id+"F0.wireOp",EDGE,"E11"),subQ23,subQ19,subQ18,subQ22,sQuery(id+"F0.wireOp",EDGE,"E20"),sQuery(id+"F0.wireOp",EDGE,"E21"),subQ15,subQ11,subQ10,subQ14,sQuery(id+"F0.wireOp",EDGE,"E30.bottom"),sQuery(id+"F0.wireOp",EDGE,"E30.top"),sQuery(id+"F0.wireOp",EDGE,"E30.left"),sQuery(id+"F0.wireOp",EDGE,"E30.right"),sQuery(id+"F0.wireOp",EDGE,"E31"),sQuery(id+"F0.wireOp",EDGE,"E32"),subQ7,subQ3,subQ2,subQ6,subQ25,subQ24,subQ29,subQ28,subQ13,subQ12,subQ9,subQ8,subQ17,subQ16,subQ21,subQ20,subQ5,subQ4,subQ1,subQ0])],"isStart":true}),makeQuery(id+"F3.opExtrude","CAP_FACE",FACE,{"disambiguationData":[OSD([subQ31,subQ30,subQ29,subQ28])],"isStart":true}),makeQuery(id+"F3.opExtrude","CAP_FACE",FACE,{"disambiguationData":[OSD([subQ27,subQ26,subQ25,subQ24])],"isStart":true}),makeQuery(id+"F3.opExtrude","CAP_FACE",FACE,{"disambiguationData":[OSD([subQ23,subQ22,subQ21,subQ20])],"isStart":true}),makeQuery(id+"F3.opExtrude","CAP_FACE",FACE,{"disambiguationData":[OSD([subQ19,subQ18,subQ17,subQ16])],"isStart":true}),makeQuery(id+"F3.opExtrude","CAP_FACE",FACE,{"disambiguationData":[OSD([subQ15,subQ14,subQ13,subQ12])],"isStart":true}),makeQuery(id+"F3.opExtrude","CAP_FACE",FACE,{"disambiguationData":[OSD([subQ11,subQ10,subQ9,subQ8])],"isStart":true}),makeQuery(id+"F3.opExtrude","CAP_FACE",FACE,{"disambiguationData":[OSD([subQ7,subQ6,subQ5,subQ4])],"isStart":true}),makeQuery(id+"F3.opExtrude","CAP_FACE",FACE,{"disambiguationData":[OSD([subQ3,subQ2,subQ1,subQ0])],"isStart":true})]});}
            var sketch = newSketch(context, id + "F17", { "sketchPlane" : qUnion([Q0])});
            skLineSegment(sketch, "E65.bottom", {"start": v(81.44, 50.52) * mm, "end": v(31.44, 50.52) * mm});
            skLineSegment(sketch, "E65.top", {"start": v(81.44, 85.52) * mm, "end": v(31.44, 85.52) * mm});
            skLineSegment(sketch, "E65.left", {"start": v(81.44, 50.52) * mm, "end": v(81.44, 85.52) * mm});
            skLineSegment(sketch, "E65.right", {"start": v(31.44, 50.52) * mm, "end": v(31.44, 85.52) * mm});
            skSolve(sketch);
        }
        {
            var Q0;
            Q0=makeQuery(id+"F17.imprint","IMPRINT",FACE,{"disambiguationData":[TD([[makeQuery(id+"F17.imprint","IMPRINT",EDGE,{"derivedFrom":sQuery(id+"F17.wireOp",EDGE,"E65.bottom")}),-1.0]])]});
            extrude(context, id + "F18", {"entities" : qUnion([Q0]), "operationType" : NewBodyOperationType.REMOVE, "oppositeDirection" : true, "depth" : 3 * mm});
        }
        {
            var Q0;
            Q0=makeQuery(id+"F18.boolean.opBoolean","MERGE",FACE,{"derivedFrom":[makeQuery(id+"F6.opExtrude","SWEPT_FACE",FACE,{"disambiguationData":[OSD([sQuery(id+"F5.wireOp",EDGE,"E57.left")])]}),makeQuery(id+"F18.opExtrude","SWEPT_FACE",FACE,{"disambiguationData":[OSD([sQuery(id+"F17.wireOp",EDGE,"E65.top")])]})]});
            var sketch = newSketch(context, id + "F19", { "sketchPlane" : qUnion([Q0])});
            skPoint(sketch, "E66", {"position": v(-33.74, -35) * mm});
            skPoint(sketch, "E67", {"position": v(-150.74, -35) * mm});
            skSolve(sketch);
        }
        {
            var Q0;
            Q0=sQuery(id+"F19.wireOp",VERTEX,"E66");
            var Q1;
            Q1=sQuery(id+"F19.wireOp",VERTEX,"E67");
            var Q2;
            Q2=makeQuery(id+"F1.opExtrude","SWEPT_BODY",BODY,{"disambiguationData":[OSD([sQuery(id+"F0.wireOp",EDGE,"E0"),sQuery(id+"F0.wireOp",EDGE,"E1"),sQuery(id+"F0.wireOp",EDGE,"E2"),sQuery(id+"F0.wireOp",EDGE,"E3"),sQuery(id+"F0.wireOp",EDGE,"E8"),sQuery(id+"F0.wireOp",EDGE,"E9"),sQuery(id+"F0.wireOp",EDGE,"E10"),sQuery(id+"F0.wireOp",EDGE,"E11"),sQuery(id+"F0.wireOp",EDGE,"E12"),sQuery(id+"F0.wireOp",EDGE,"E13"),sQuery(id+"F0.wireOp",EDGE,"E18"),sQuery(id+"F0.wireOp",EDGE,"E19"),sQuery(id+"F0.wireOp",EDGE,"E20"),sQuery(id+"F0.wireOp",EDGE,"E21"),sQuery(id+"F0.wireOp",EDGE,"E22"),sQuery(id+"F0.wireOp",EDGE,"E23"),sQuery(id+"F0.wireOp",EDGE,"E28"),sQuery(id+"F0.wireOp",EDGE,"E29"),sQuery(id+"F0.wireOp",EDGE,"E30.bottom"),sQuery(id+"F0.wireOp",EDGE,"E30.top"),sQuery(id+"F0.wireOp",EDGE,"E30.left"),sQuery(id+"F0.wireOp",EDGE,"E30.right"),sQuery(id+"F0.wireOp",EDGE,"E31"),sQuery(id+"F0.wireOp",EDGE,"E32"),sQuery(id+"F0.wireOp",EDGE,"E33"),sQuery(id+"F0.wireOp",EDGE,"E34"),sQuery(id+"F0.wireOp",EDGE,"E39"),sQuery(id+"F0.wireOp",EDGE,"E40"),sQuery(id+"F0.wireOp",EDGE,"E41"),sQuery(id+"F0.wireOp",EDGE,"E42"),sQuery(id+"F0.wireOp",EDGE,"E43"),sQuery(id+"F0.wireOp",EDGE,"E44"),sQuery(id+"F0.wireOp",EDGE,"E45"),sQuery(id+"F0.wireOp",EDGE,"E46"),sQuery(id+"F0.wireOp",EDGE,"E47"),sQuery(id+"F0.wireOp",EDGE,"E48"),sQuery(id+"F0.wireOp",EDGE,"E49"),sQuery(id+"F0.wireOp",EDGE,"E50"),sQuery(id+"F0.wireOp",EDGE,"E51"),sQuery(id+"F0.wireOp",EDGE,"E52"),sQuery(id+"F0.wireOp",EDGE,"E53"),sQuery(id+"F0.wireOp",EDGE,"E54"),sQuery(id+"F0.wireOp",EDGE,"E55"),sQuery(id+"F0.wireOp",EDGE,"E56")])]});
            hole(context, id + "F20", {"style" : HoleStyle.SIMPLE, "endStyle" : HoleEndStyle.THROUGH, "holeDiameter" : 5 * mm, "locations" : qUnion([Q0, Q1]), "scope" : qUnion([Q2]), "isTappedThrough" : true});
        }
        {
            var Q0;
            Q0=makeQuery(id+"F18.boolean.opBoolean","MERGE",FACE,{"derivedFrom":[makeQuery(id+"F6.opExtrude","SWEPT_FACE",FACE,{"disambiguationData":[OSD([sQuery(id+"F5.wireOp",EDGE,"E57.left")])]}),makeQuery(id+"F18.opExtrude","SWEPT_FACE",FACE,{"disambiguationData":[OSD([sQuery(id+"F17.wireOp",EDGE,"E65.top")])]})]});
            var sketch = newSketch(context, id + "F21", { "sketchPlane" : qUnion([Q0])});
            skText(sketch, "E68", { "text": "RiCkY", "fontName": "OpenSans-Bold.ttf"});
            const initialGuessF21  = {"E68": [-0.1352, -0.01067, 1, 0, 0.00885]};
            skSetInitialGuess(sketch, initialGuessF21);
            skSolve(sketch);
        }
        {
            var Q0;
            Q0 = qSketchRegion(id + "F21", true);
            extrude(context, id + "F22", {"entities" : qUnion([Q0]), "operationType" : NewBodyOperationType.ADD, "depth" : 1 * mm});
        }
        {
            var Q0;
            Q0=makeQuery(id+"F12.boolean.opBoolean","COPY",FACE,{"derivedFrom":makeQuery(id+"F12.opExtrude","SWEPT_FACE",FACE,{"disambiguationData":[OSD([sQuery(id+"F11.wireOp",EDGE,"E62.top")])]})});
            extrude(context, id + "F23", {"entities" : qUnion([Q0]), "operationType" : NewBodyOperationType.ADD, "depth" : 2 * mm});
        }
        {
            var Q0;
            {var subQ0=sQuery(id+"F11.wireOp",EDGE,"E62.top");var subQ26=sQuery(id+"F0.wireOp",EDGE,"E30.bottom");var subQ46=sQuery(id+"F5.wireOp",EDGE,"E57.left");Q0=makeQuery(id+"F23.boolean.opBoolean","MERGE",FACE,{"derivedFrom":[makeQuery(id+"F22.boolean.opBoolean","SPLIT",FACE,{"disambiguationData":[TD([makeQuery(id+"F1.opExtrude","SWEPT_FACE",FACE,{"disambiguationData":[OSD([subQ26])]})])],"derivedFrom":makeQuery(id+"F18.boolean.opBoolean","MERGE",FACE,{"derivedFrom":[makeQuery(id+"F6.opExtrude","SWEPT_FACE",FACE,{"disambiguationData":[OSD([subQ46])]}),makeQuery(id+"F18.opExtrude","SWEPT_FACE",FACE,{"disambiguationData":[OSD([sQuery(id+"F17.wireOp",EDGE,"E65.top")])]})]})}),makeQuery(id+"F23.opExtrude","SWEPT_FACE",FACE,{"disambiguationData":[OSD([subQ0]),TDD([makeQuery(id+"F12.boolean.opBoolean","COPY",EDGE,{"derivedFrom":makeQuery(id+"F12.opExtrude","CAP_EDGE",EDGE,{"disambiguationData":[OSD([subQ0])],"isStart":true})})])]})]});}
            var sketch = newSketch(context, id + "F24", { "sketchPlane" : qUnion([Q0])});
            skLineSegment(sketch, "E69.bottom", {"start": v(-156.74, -50) * mm, "end": v(-31.74, -50) * mm});
            skLineSegment(sketch, "E69.top", {"start": v(-156.74, -60) * mm, "end": v(-31.74, -60) * mm});
            skLineSegment(sketch, "E69.left", {"start": v(-156.74, -50) * mm, "end": v(-156.74, -60) * mm});
            skLineSegment(sketch, "E69.right", {"start": v(-31.74, -50) * mm, "end": v(-31.74, -60) * mm});
            skSolve(sketch);
        }
        {
            var Q0;
            Q0=makeQuery(id+"F24.imprint","IMPRINT",FACE,{"disambiguationData":[TD([[makeQuery(id+"F24.imprint","IMPRINT",EDGE,{"derivedFrom":sQuery(id+"F24.wireOp",EDGE,"E69.top")}),1.0]])]});
            extrude(context, id + "F25", {"entities" : qUnion([Q0]), "operationType" : NewBodyOperationType.ADD, "depth" : 14 * mm});
        }
        {
            var Q0;
            Q0=makeQuery(id+"F25.opExtrude","CAP_FACE",FACE,{"disambiguationData":[OSD([sQuery(id+"F24.wireOp",EDGE,"E69.bottom"),sQuery(id+"F24.wireOp",EDGE,"E69.top"),sQuery(id+"F24.wireOp",EDGE,"E69.left"),sQuery(id+"F24.wireOp",EDGE,"E69.right")])],"isStart":false});
            var sketch = newSketch(context, id + "F26", { "sketchPlane" : qUnion([Q0])});
            skLineSegment(sketch, "E70.bottom", {"start": v(-151.74, -50) * mm, "end": v(-146.74, -50) * mm});
            skLineSegment(sketch, "E70.top", {"start": v(-151.74, -60) * mm, "end": v(-146.74, -60) * mm});
            skLineSegment(sketch, "E70.left", {"start": v(-151.74, -50) * mm, "end": v(-151.74, -60) * mm});
            skLineSegment(sketch, "E70.right", {"start": v(-146.74, -50) * mm, "end": v(-146.74, -60) * mm});
            skLineSegment(sketch, "E71.bottom", {"start": v(-134.74, -50) * mm, "end": v(-129.74, -50) * mm});
            skLineSegment(sketch, "E71.top", {"start": v(-134.74, -60) * mm, "end": v(-129.74, -60) * mm});
            skLineSegment(sketch, "E71.left", {"start": v(-134.74, -50) * mm, "end": v(-134.74, -60) * mm});
            skLineSegment(sketch, "E71.right", {"start": v(-129.74, -50) * mm, "end": v(-129.74, -60) * mm});
            skLineSegment(sketch, "E72.bottom", {"start": v(-117.74, -50) * mm, "end": v(-112.74, -50) * mm});
            skLineSegment(sketch, "E72.top", {"start": v(-117.74, -60) * mm, "end": v(-112.74, -60) * mm});
            skLineSegment(sketch, "E72.left", {"start": v(-117.74, -50) * mm, "end": v(-117.74, -60) * mm});
            skLineSegment(sketch, "E72.right", {"start": v(-112.74, -50) * mm, "end": v(-112.74, -60) * mm});
            skLineSegment(sketch, "E73.bottom", {"start": v(-100.74, -50) * mm, "end": v(-95.74, -50) * mm});
            skLineSegment(sketch, "E73.top", {"start": v(-100.74, -60) * mm, "end": v(-95.74, -60) * mm});
            skLineSegment(sketch, "E73.left", {"start": v(-100.74, -50) * mm, "end": v(-100.74, -60) * mm});
            skLineSegment(sketch, "E73.right", {"start": v(-95.74, -50) * mm, "end": v(-95.74, -60) * mm});
            skLineSegment(sketch, "E74.bottom", {"start": v(-77.74, -50) * mm, "end": v(-62.74, -50) * mm});
            skLineSegment(sketch, "E74.top", {"start": v(-77.74, -60) * mm, "end": v(-62.74, -60) * mm});
            skLineSegment(sketch, "E74.left", {"start": v(-77.74, -50) * mm, "end": v(-77.74, -60) * mm});
            skLineSegment(sketch, "E74.right", {"start": v(-62.74, -50) * mm, "end": v(-62.74, -60) * mm});
            skLineSegment(sketch, "E75.bottom", {"start": v(-52.74, -50) * mm, "end": v(-37.74, -50) * mm});
            skLineSegment(sketch, "E75.top", {"start": v(-52.74, -60) * mm, "end": v(-37.74, -60) * mm});
            skLineSegment(sketch, "E75.left", {"start": v(-52.74, -50) * mm, "end": v(-52.74, -60) * mm});
            skLineSegment(sketch, "E75.right", {"start": v(-37.74, -50) * mm, "end": v(-37.74, -60) * mm});
            skSolve(sketch);
        }
        {
            var Q0;
            Q0=makeQuery(id+"F26.imprint","IMPRINT",FACE,{"disambiguationData":[TD([[makeQuery(id+"F26.imprint","IMPRINT",EDGE,{"derivedFrom":sQuery(id+"F26.wireOp",EDGE,"E73.bottom")}),-1.0]])]});
            var Q1;
            Q1=makeQuery(id+"F26.imprint","IMPRINT",FACE,{"disambiguationData":[TD([[makeQuery(id+"F26.imprint","IMPRINT",EDGE,{"derivedFrom":sQuery(id+"F26.wireOp",EDGE,"E72.bottom")}),-1.0]])]});
            var Q2;
            Q2=makeQuery(id+"F26.imprint","IMPRINT",FACE,{"disambiguationData":[TD([[makeQuery(id+"F26.imprint","IMPRINT",EDGE,{"derivedFrom":sQuery(id+"F26.wireOp",EDGE,"E71.bottom")}),-1.0]])]});
            var Q3;
            Q3=makeQuery(id+"F26.imprint","IMPRINT",FACE,{"disambiguationData":[TD([[makeQuery(id+"F26.imprint","IMPRINT",EDGE,{"derivedFrom":sQuery(id+"F26.wireOp",EDGE,"E70.bottom")}),-1.0]])]});
            extrude(context, id + "F27", {"entities" : qUnion([Q0, Q1, Q2, Q3]), "operationType" : NewBodyOperationType.ADD, "depth" : 7 * mm});
        }
        {
            var Q0;
            Q0=makeQuery(id+"F26.imprint","IMPRINT",FACE,{"disambiguationData":[TD([[makeQuery(id+"F26.imprint","IMPRINT",EDGE,{"derivedFrom":sQuery(id+"F26.wireOp",EDGE,"E74.bottom")}),-1.0]])]});
            var Q1;
            Q1=makeQuery(id+"F26.imprint","IMPRINT",FACE,{"disambiguationData":[TD([[makeQuery(id+"F26.imprint","IMPRINT",EDGE,{"derivedFrom":sQuery(id+"F26.wireOp",EDGE,"E75.bottom")}),-1.0]])]});
            extrude(context, id + "F28", {"entities" : qUnion([Q0, Q1]), "operationType" : NewBodyOperationType.ADD, "depth" : 5 * mm});
        }
        {
            var Q0;
            Q0=makeQuery(id+"F28.opExtrude","CAP_FACE",FACE,{"disambiguationData":[OSD([sQuery(id+"F26.wireOp",EDGE,"E74.bottom"),sQuery(id+"F26.wireOp",EDGE,"E74.top"),sQuery(id+"F26.wireOp",EDGE,"E74.left"),sQuery(id+"F26.wireOp",EDGE,"E74.right")])],"isStart":false});
            var sketch = newSketch(context, id + "F29", { "sketchPlane" : qUnion([Q0])});
            skLineSegment(sketch, "E76.bottom", {"start": v(-77.74, -50) * mm, "end": v(-72.74, -50) * mm});
            skLineSegment(sketch, "E76.top", {"start": v(-77.74, -60) * mm, "end": v(-72.74, -60) * mm});
            skLineSegment(sketch, "E76.left", {"start": v(-77.74, -50) * mm, "end": v(-77.74, -60) * mm});
            skLineSegment(sketch, "E76.right", {"start": v(-72.74, -50) * mm, "end": v(-72.74, -60) * mm});
            skSolve(sketch);
        }
        {
            var Q0;
            Q0=makeQuery(id+"F28.opExtrude","CAP_FACE",FACE,{"disambiguationData":[OSD([sQuery(id+"F26.wireOp",EDGE,"E75.bottom"),sQuery(id+"F26.wireOp",EDGE,"E75.top"),sQuery(id+"F26.wireOp",EDGE,"E75.left"),sQuery(id+"F26.wireOp",EDGE,"E75.right")])],"isStart":false});
            var sketch = newSketch(context, id + "F30", { "sketchPlane" : qUnion([Q0])});
            skLineSegment(sketch, "E77.bottom", {"start": v(-52.74, -50) * mm, "end": v(-47.74, -50) * mm});
            skLineSegment(sketch, "E77.top", {"start": v(-52.74, -60) * mm, "end": v(-47.74, -60) * mm});
            skLineSegment(sketch, "E77.left", {"start": v(-52.74, -50) * mm, "end": v(-52.74, -60) * mm});
            skLineSegment(sketch, "E77.right", {"start": v(-47.74, -50) * mm, "end": v(-47.74, -60) * mm});
            skSolve(sketch);
        }
        {
            var Q0;
            Q0=makeQuery(id+"F30.imprint","IMPRINT",FACE,{"disambiguationData":[TD([[makeQuery(id+"F30.imprint","IMPRINT",EDGE,{"derivedFrom":sQuery(id+"F30.wireOp",EDGE,"E77.bottom")}),-1.0]])]});
            var Q1;
            Q1=makeQuery(id+"F29.imprint","IMPRINT",FACE,{"disambiguationData":[TD([[makeQuery(id+"F29.imprint","IMPRINT",EDGE,{"derivedFrom":sQuery(id+"F29.wireOp",EDGE,"E76.bottom")}),-1.0]])]});
            extrude(context, id + "F31", {"entities" : qUnion([Q0, Q1]), "operationType" : NewBodyOperationType.ADD, "depth" : 7 * mm});
        }
        {
            var Q0;
            Q0=makeQuery(id+"F27.opExtrude","SWEPT_FACE",FACE,{"disambiguationData":[OSD([sQuery(id+"F26.wireOp",EDGE,"E70.left")])]});
            var sketch = newSketch(context, id + "F32", { "sketchPlane" : qUnion([Q0])});
            skLineSegment(sketch, "E78.bottom", {"start": v(-71.52, -53) * mm, "end": v(-67.52, -53) * mm});
            skLineSegment(sketch, "E78.top", {"start": v(-71.52, -57) * mm, "end": v(-67.52, -57) * mm});
            skLineSegment(sketch, "E78.left", {"start": v(-71.52, -53) * mm, "end": v(-71.52, -57) * mm});
            skLineSegment(sketch, "E78.right", {"start": v(-67.52, -53) * mm, "end": v(-67.52, -57) * mm});
            skSolve(sketch);
        }
        {
            var Q0;
            Q0=makeQuery(id+"F32.imprint","IMPRINT",FACE,{"disambiguationData":[TD([[makeQuery(id+"F32.imprint","IMPRINT",EDGE,{"derivedFrom":sQuery(id+"F32.wireOp",EDGE,"E78.bottom")}),-1.0]])]});
            extrude(context, id + "F33", {"entities" : qUnion([Q0]), "operationType" : NewBodyOperationType.REMOVE, "oppositeDirection" : true, "depth" : 65 * mm});
        }
        {
            var Q0;
            Q0=makeQuery(id+"F27.opExtrude","CAP_EDGE",EDGE,{"disambiguationData":[OSD([sQuery(id+"F26.wireOp",EDGE,"E71.top")])],"isStart":false});
            var Q1;
            Q1=makeQuery(id+"F27.opExtrude","CAP_EDGE",EDGE,{"disambiguationData":[OSD([sQuery(id+"F26.wireOp",EDGE,"E71.bottom")])],"isStart":false});
            var Q2;
            Q2=makeQuery(id+"F27.opExtrude","CAP_EDGE",EDGE,{"disambiguationData":[OSD([sQuery(id+"F26.wireOp",EDGE,"E70.top")])],"isStart":false});
            var Q3;
            Q3=makeQuery(id+"F27.opExtrude","CAP_EDGE",EDGE,{"disambiguationData":[OSD([sQuery(id+"F26.wireOp",EDGE,"E70.bottom")])],"isStart":false});
            var Q4;
            Q4=makeQuery(id+"F27.opExtrude","CAP_EDGE",EDGE,{"disambiguationData":[OSD([sQuery(id+"F26.wireOp",EDGE,"E72.top")])],"isStart":false});
            var Q5;
            Q5=makeQuery(id+"F27.opExtrude","CAP_EDGE",EDGE,{"disambiguationData":[OSD([sQuery(id+"F26.wireOp",EDGE,"E72.bottom")])],"isStart":false});
            var Q6;
            Q6=makeQuery(id+"F27.opExtrude","CAP_EDGE",EDGE,{"disambiguationData":[OSD([sQuery(id+"F26.wireOp",EDGE,"E73.top")])],"isStart":false});
            var Q7;
            Q7=makeQuery(id+"F27.opExtrude","CAP_EDGE",EDGE,{"disambiguationData":[OSD([sQuery(id+"F26.wireOp",EDGE,"E73.bottom")])],"isStart":false});
            var Q8;
            {var subQ0=sQuery(id+"F26.wireOp",EDGE,"E73.left");var subQ1=sQuery(id+"F24.wireOp",EDGE,"E69.top");Q8=makeQuery(id+"F33.boolean.opBoolean","SPLIT",EDGE,{"disambiguationData":[TD([makeQuery(id+"F25.opExtrude","SWEPT_FACE",FACE,{"disambiguationData":[OSD([subQ1])]})])],"derivedFrom":makeQuery(id+"F27.opExtrude","CAP_EDGE",EDGE,{"disambiguationData":[OSD([subQ0])],"isStart":true})});}
            var Q9;
            {var subQ0=sQuery(id+"F26.wireOp",EDGE,"E73.left");Q9=makeQuery(id+"F33.boolean.opBoolean","SPLIT",EDGE,{"disambiguationData":[TD([makeQuery(id+"F23.opExtrude","CAP_FACE",FACE,{"disambiguationData":[OSD([sQuery(id+"F11.wireOp",EDGE,"E62.top")])],"isStart":false})])],"derivedFrom":makeQuery(id+"F27.opExtrude","CAP_EDGE",EDGE,{"disambiguationData":[OSD([subQ0])],"isStart":true})});}
            var Q10;
            {var subQ0=sQuery(id+"F26.wireOp",EDGE,"E72.left");var subQ1=sQuery(id+"F24.wireOp",EDGE,"E69.top");Q10=makeQuery(id+"F33.boolean.opBoolean","SPLIT",EDGE,{"disambiguationData":[TD([makeQuery(id+"F25.opExtrude","SWEPT_FACE",FACE,{"disambiguationData":[OSD([subQ1])]})])],"derivedFrom":makeQuery(id+"F27.opExtrude","CAP_EDGE",EDGE,{"disambiguationData":[OSD([subQ0])],"isStart":true})});}
            var Q11;
            {var subQ1=sQuery(id+"F26.wireOp",EDGE,"E72.left");Q11=makeQuery(id+"F33.boolean.opBoolean","SPLIT",EDGE,{"disambiguationData":[TD([makeQuery(id+"F23.opExtrude","CAP_FACE",FACE,{"disambiguationData":[OSD([sQuery(id+"F11.wireOp",EDGE,"E62.top")])],"isStart":false})])],"derivedFrom":makeQuery(id+"F27.opExtrude","CAP_EDGE",EDGE,{"disambiguationData":[OSD([subQ1])],"isStart":true})});}
            var Q12;
            {var subQ0=sQuery(id+"F24.wireOp",EDGE,"E69.top");var subQ1=sQuery(id+"F26.wireOp",EDGE,"E71.left");Q12=makeQuery(id+"F33.boolean.opBoolean","SPLIT",EDGE,{"disambiguationData":[TD([makeQuery(id+"F25.opExtrude","SWEPT_FACE",FACE,{"disambiguationData":[OSD([subQ0])]})])],"derivedFrom":makeQuery(id+"F27.opExtrude","CAP_EDGE",EDGE,{"disambiguationData":[OSD([subQ1])],"isStart":true})});}
            var Q13;
            {var subQ0=sQuery(id+"F26.wireOp",EDGE,"E71.left");Q13=makeQuery(id+"F33.boolean.opBoolean","SPLIT",EDGE,{"disambiguationData":[TD([makeQuery(id+"F23.opExtrude","CAP_FACE",FACE,{"disambiguationData":[OSD([sQuery(id+"F11.wireOp",EDGE,"E62.top")])],"isStart":false})])],"derivedFrom":makeQuery(id+"F27.opExtrude","CAP_EDGE",EDGE,{"disambiguationData":[OSD([subQ0])],"isStart":true})});}
            var Q14;
            {var subQ0=sQuery(id+"F26.wireOp",EDGE,"E70.left");var subQ1=sQuery(id+"F24.wireOp",EDGE,"E69.top");Q14=makeQuery(id+"F33.boolean.opBoolean","SPLIT",EDGE,{"disambiguationData":[TD([makeQuery(id+"F25.opExtrude","SWEPT_FACE",FACE,{"disambiguationData":[OSD([subQ1])]})])],"derivedFrom":makeQuery(id+"F27.opExtrude","CAP_EDGE",EDGE,{"disambiguationData":[OSD([subQ0])],"isStart":true})});}
            var Q15;
            {var subQ0=sQuery(id+"F26.wireOp",EDGE,"E70.left");Q15=makeQuery(id+"F33.boolean.opBoolean","SPLIT",EDGE,{"disambiguationData":[TD([makeQuery(id+"F23.opExtrude","CAP_FACE",FACE,{"disambiguationData":[OSD([sQuery(id+"F11.wireOp",EDGE,"E62.top")])],"isStart":false})])],"derivedFrom":makeQuery(id+"F27.opExtrude","CAP_EDGE",EDGE,{"disambiguationData":[OSD([subQ0])],"isStart":true})});}
            var Q16;
            {var subQ0=sQuery(id+"F26.wireOp",EDGE,"E73.right");Q16=makeQuery(id+"F33.boolean.opBoolean","SPLIT",EDGE,{"disambiguationData":[TD([makeQuery(id+"F23.opExtrude","CAP_FACE",FACE,{"disambiguationData":[OSD([sQuery(id+"F11.wireOp",EDGE,"E62.top")])],"isStart":false})])],"derivedFrom":makeQuery(id+"F27.opExtrude","CAP_EDGE",EDGE,{"disambiguationData":[OSD([subQ0])],"isStart":true})});}
            var Q17;
            {var subQ0=sQuery(id+"F26.wireOp",EDGE,"E73.right");var subQ1=sQuery(id+"F24.wireOp",EDGE,"E69.top");Q17=makeQuery(id+"F33.boolean.opBoolean","SPLIT",EDGE,{"disambiguationData":[TD([makeQuery(id+"F25.opExtrude","SWEPT_FACE",FACE,{"disambiguationData":[OSD([subQ1])]})])],"derivedFrom":makeQuery(id+"F27.opExtrude","CAP_EDGE",EDGE,{"disambiguationData":[OSD([subQ0])],"isStart":true})});}
            var Q18;
            {var subQ0=sQuery(id+"F26.wireOp",EDGE,"E72.right");Q18=makeQuery(id+"F33.boolean.opBoolean","SPLIT",EDGE,{"disambiguationData":[TD([makeQuery(id+"F23.opExtrude","CAP_FACE",FACE,{"disambiguationData":[OSD([sQuery(id+"F11.wireOp",EDGE,"E62.top")])],"isStart":false})])],"derivedFrom":makeQuery(id+"F27.opExtrude","CAP_EDGE",EDGE,{"disambiguationData":[OSD([subQ0])],"isStart":true})});}
            var Q19;
            {var subQ0=sQuery(id+"F26.wireOp",EDGE,"E72.right");var subQ1=sQuery(id+"F24.wireOp",EDGE,"E69.top");Q19=makeQuery(id+"F33.boolean.opBoolean","SPLIT",EDGE,{"disambiguationData":[TD([makeQuery(id+"F25.opExtrude","SWEPT_FACE",FACE,{"disambiguationData":[OSD([subQ1])]})])],"derivedFrom":makeQuery(id+"F27.opExtrude","CAP_EDGE",EDGE,{"disambiguationData":[OSD([subQ0])],"isStart":true})});}
            var Q20;
            {var subQ0=sQuery(id+"F26.wireOp",EDGE,"E71.right");Q20=makeQuery(id+"F33.boolean.opBoolean","SPLIT",EDGE,{"disambiguationData":[TD([makeQuery(id+"F23.opExtrude","CAP_FACE",FACE,{"disambiguationData":[OSD([sQuery(id+"F11.wireOp",EDGE,"E62.top")])],"isStart":false})])],"derivedFrom":makeQuery(id+"F27.opExtrude","CAP_EDGE",EDGE,{"disambiguationData":[OSD([subQ0])],"isStart":true})});}
            var Q21;
            {var subQ0=sQuery(id+"F26.wireOp",EDGE,"E71.right");var subQ1=sQuery(id+"F24.wireOp",EDGE,"E69.top");Q21=makeQuery(id+"F33.boolean.opBoolean","SPLIT",EDGE,{"disambiguationData":[TD([makeQuery(id+"F25.opExtrude","SWEPT_FACE",FACE,{"disambiguationData":[OSD([subQ1])]})])],"derivedFrom":makeQuery(id+"F27.opExtrude","CAP_EDGE",EDGE,{"disambiguationData":[OSD([subQ0])],"isStart":true})});}
            var Q22;
            {var subQ0=sQuery(id+"F26.wireOp",EDGE,"E70.right");Q22=makeQuery(id+"F33.boolean.opBoolean","SPLIT",EDGE,{"disambiguationData":[TD([makeQuery(id+"F23.opExtrude","CAP_FACE",FACE,{"disambiguationData":[OSD([sQuery(id+"F11.wireOp",EDGE,"E62.top")])],"isStart":false})])],"derivedFrom":makeQuery(id+"F27.opExtrude","CAP_EDGE",EDGE,{"disambiguationData":[OSD([subQ0])],"isStart":true})});}
            var Q23;
            {var subQ0=sQuery(id+"F26.wireOp",EDGE,"E70.right");var subQ1=sQuery(id+"F24.wireOp",EDGE,"E69.top");Q23=makeQuery(id+"F33.boolean.opBoolean","SPLIT",EDGE,{"disambiguationData":[TD([makeQuery(id+"F25.opExtrude","SWEPT_FACE",FACE,{"disambiguationData":[OSD([subQ1])]})])],"derivedFrom":makeQuery(id+"F27.opExtrude","CAP_EDGE",EDGE,{"disambiguationData":[OSD([subQ0])],"isStart":true})});}
            var Q24;
            Q24=makeQuery(id+"F31.opExtrude","CAP_EDGE",EDGE,{"disambiguationData":[OSD([sQuery(id+"F29.wireOp",EDGE,"E76.top")])],"isStart":false});
            var Q25;
            Q25=makeQuery(id+"F31.opExtrude","CAP_EDGE",EDGE,{"disambiguationData":[OSD([sQuery(id+"F29.wireOp",EDGE,"E76.bottom")])],"isStart":false});
            var Q26;
            Q26=makeQuery(id+"F31.opExtrude","CAP_EDGE",EDGE,{"disambiguationData":[OSD([sQuery(id+"F30.wireOp",EDGE,"E77.top")])],"isStart":false});
            var Q27;
            Q27=makeQuery(id+"F31.opExtrude","CAP_EDGE",EDGE,{"disambiguationData":[OSD([sQuery(id+"F30.wireOp",EDGE,"E77.bottom")])],"isStart":false});
            var Q28;
            Q28=makeQuery(id+"F31.opExtrude","CAP_EDGE",EDGE,{"disambiguationData":[OSD([sQuery(id+"F29.wireOp",EDGE,"E76.right")])],"isStart":true});
            var Q29;
            Q29=makeQuery(id+"F31.opExtrude","CAP_EDGE",EDGE,{"disambiguationData":[OSD([sQuery(id+"F30.wireOp",EDGE,"E77.right")])],"isStart":true});
            fillet(context, id + "F34", {"entities" : qUnion([Q0, Q1, Q2, Q3, Q4, Q5, Q6, Q7, Q8, Q9, Q10, Q11, Q12, Q13, Q14, Q15, Q16, Q17, Q18, Q19, Q20, Q21, Q22, Q23, Q24, Q25, Q26, Q27, Q28, Q29]), "radius" : 2 * mm, "tangentPropagation" : true, "allowEdgeOverflow" : false});
        }
        {
            var Q0;
            Q0=makeQuery(id+"F31.opExtrude","SWEPT_FACE",FACE,{"disambiguationData":[OSD([sQuery(id+"F30.wireOp",EDGE,"E77.right")])]});
            var sketch = newSketch(context, id + "F35", { "sketchPlane" : qUnion([Q0])});
            skLineSegment(sketch, "E79.bottom", {"start": v(62.52, -53) * mm, "end": v(66.52, -53) * mm});
            skLineSegment(sketch, "E79.top", {"start": v(62.52, -57) * mm, "end": v(66.52, -57) * mm});
            skLineSegment(sketch, "E79.left", {"start": v(62.52, -53) * mm, "end": v(62.52, -57) * mm});
            skLineSegment(sketch, "E79.right", {"start": v(66.52, -53) * mm, "end": v(66.52, -57) * mm});
            skSolve(sketch);
        }
        {
            var Q0;
            {var subQ0=sQuery(id+"F35.wireOp",EDGE,"E79.left");Q0=makeQuery(id+"F35.imprint","IMPRINT",FACE,{"disambiguationData":[TD([[makeQuery(id+"F35.imprint","IMPRINT",EDGE,{"derivedFrom":subQ0}),1.0]])]});}
            var Q1;
            {var subQ0=sQuery(id+"F35.wireOp",EDGE,"E79.right");Q1=makeQuery(id+"F35.imprint","IMPRINT",FACE,{"disambiguationData":[TD([[makeQuery(id+"F35.imprint","IMPRINT",EDGE,{"derivedFrom":subQ0}),-1.0]])]});}
            extrude(context, id + "F36", {"entities" : qUnion([Q0, Q1]), "operationType" : NewBodyOperationType.REMOVE, "oppositeDirection" : true, "depth" : 35 * mm, "hasSecondDirection" : true, "secondDirectionOppositeDirection" : false, "secondDirectionDepth" : 25 * mm});
        }
        {
            var Q0;
            Q0=makeQuery(id+"F28.opExtrude","CAP_EDGE",EDGE,{"disambiguationData":[OSD([sQuery(id+"F26.wireOp",EDGE,"E74.right")])],"isStart":false});
            var Q1;
            Q1=makeQuery(id+"F28.opExtrude","CAP_EDGE",EDGE,{"disambiguationData":[OSD([sQuery(id+"F26.wireOp",EDGE,"E75.right")])],"isStart":false});
            fillet(context, id + "F37", {"entities" : qUnion([Q0, Q1]), "radius" : 1.81 * mm, "tangentPropagation" : true, "allowEdgeOverflow" : false});
        }
        {
            var Q0;
            Q0=makeQuery(id+"F31.boolean.opBoolean","MERGE",FACE,{"derivedFrom":[makeQuery(id+"F28.boolean.opBoolean","MERGE",FACE,{"derivedFrom":[makeQuery(id+"F27.boolean.opBoolean","MERGE",FACE,{"derivedFrom":[makeQuery(id+"F25.boolean.opBoolean","MERGE",FACE,{"derivedFrom":[makeQuery(id+"F6.opExtrude","CAP_FACE",FACE,{"disambiguationData":[OSD([sQuery(id+"F5.wireOp",EDGE,"E57.bottom"),sQuery(id+"F5.wireOp",EDGE,"E57.top"),sQuery(id+"F5.wireOp",EDGE,"E57.left"),sQuery(id+"F5.wireOp",EDGE,"E57.right")])],"isStart":false}),makeQuery(id+"F25.opExtrude","SWEPT_FACE",FACE,{"disambiguationData":[OSD([sQuery(id+"F24.wireOp",EDGE,"E69.top")])]})]}),makeQuery(id+"F27.opExtrude","SWEPT_FACE",FACE,{"disambiguationData":[OSD([sQuery(id+"F26.wireOp",EDGE,"E70.top")])]}),makeQuery(id+"F27.opExtrude","SWEPT_FACE",FACE,{"disambiguationData":[OSD([sQuery(id+"F26.wireOp",EDGE,"E71.top")])]}),makeQuery(id+"F27.opExtrude","SWEPT_FACE",FACE,{"disambiguationData":[OSD([sQuery(id+"F26.wireOp",EDGE,"E72.top")])]}),makeQuery(id+"F27.opExtrude","SWEPT_FACE",FACE,{"disambiguationData":[OSD([sQuery(id+"F26.wireOp",EDGE,"E73.top")])]})]}),makeQuery(id+"F28.opExtrude","SWEPT_FACE",FACE,{"disambiguationData":[OSD([sQuery(id+"F26.wireOp",EDGE,"E74.top")])]}),makeQuery(id+"F28.opExtrude","SWEPT_FACE",FACE,{"disambiguationData":[OSD([sQuery(id+"F26.wireOp",EDGE,"E75.top")])]})]}),makeQuery(id+"F31.opExtrude","SWEPT_FACE",FACE,{"disambiguationData":[OSD([sQuery(id+"F29.wireOp",EDGE,"E76.top")])]}),makeQuery(id+"F31.opExtrude","SWEPT_FACE",FACE,{"disambiguationData":[OSD([sQuery(id+"F30.wireOp",EDGE,"E77.top")])]})]});
            var sketch = newSketch(context, id + "F38", { "sketchPlane" : qUnion([Q0])});
            skLineSegment(sketch, "E80.bottom", {"start": v(43.74, 85.52) * mm, "end": v(144.74, 85.52) * mm});
            skLineSegment(sketch, "E80.top", {"start": v(43.74, 78.52) * mm, "end": v(144.74, 78.52) * mm});
            skLineSegment(sketch, "E80.left", {"start": v(43.74, 85.52) * mm, "end": v(43.74, 78.52) * mm});
            skLineSegment(sketch, "E80.right", {"start": v(144.74, 85.52) * mm, "end": v(144.74, 78.52) * mm});
            skSolve(sketch);
        }
        {
            var Q0;
            Q0=makeQuery(id+"F38.imprint","IMPRINT",FACE,{"disambiguationData":[TD([[makeQuery(id+"F38.imprint","IMPRINT",EDGE,{"derivedFrom":sQuery(id+"F38.wireOp",EDGE,"E80.bottom")}),-1.0]])]});
            extrude(context, id + "F39", {"entities" : qUnion([Q0]), "operationType" : NewBodyOperationType.REMOVE, "oppositeDirection" : true, "depth" : 25 * mm});
        }
        {
            var Q0;
            Q0=makeQuery(id+"F1.opExtrude","CAP_FACE",FACE,{"disambiguationData":[OSD([sQuery(id+"F0.wireOp",EDGE,"E0"),sQuery(id+"F0.wireOp",EDGE,"E1"),sQuery(id+"F0.wireOp",EDGE,"E2"),sQuery(id+"F0.wireOp",EDGE,"E3"),sQuery(id+"F0.wireOp",EDGE,"E8"),sQuery(id+"F0.wireOp",EDGE,"E9"),sQuery(id+"F0.wireOp",EDGE,"E10"),sQuery(id+"F0.wireOp",EDGE,"E11"),sQuery(id+"F0.wireOp",EDGE,"E12"),sQuery(id+"F0.wireOp",EDGE,"E13"),sQuery(id+"F0.wireOp",EDGE,"E18"),sQuery(id+"F0.wireOp",EDGE,"E19"),sQuery(id+"F0.wireOp",EDGE,"E20"),sQuery(id+"F0.wireOp",EDGE,"E21"),sQuery(id+"F0.wireOp",EDGE,"E22"),sQuery(id+"F0.wireOp",EDGE,"E23"),sQuery(id+"F0.wireOp",EDGE,"E28"),sQuery(id+"F0.wireOp",EDGE,"E29"),sQuery(id+"F0.wireOp",EDGE,"E30.bottom"),sQuery(id+"F0.wireOp",EDGE,"E30.top"),sQuery(id+"F0.wireOp",EDGE,"E30.left"),sQuery(id+"F0.wireOp",EDGE,"E30.right"),sQuery(id+"F0.wireOp",EDGE,"E31"),sQuery(id+"F0.wireOp",EDGE,"E32"),sQuery(id+"F0.wireOp",EDGE,"E33"),sQuery(id+"F0.wireOp",EDGE,"E34"),sQuery(id+"F0.wireOp",EDGE,"E39"),sQuery(id+"F0.wireOp",EDGE,"E40"),sQuery(id+"F0.wireOp",EDGE,"E41"),sQuery(id+"F0.wireOp",EDGE,"E42"),sQuery(id+"F0.wireOp",EDGE,"E43"),sQuery(id+"F0.wireOp",EDGE,"E44"),sQuery(id+"F0.wireOp",EDGE,"E45"),sQuery(id+"F0.wireOp",EDGE,"E46"),sQuery(id+"F0.wireOp",EDGE,"E47"),sQuery(id+"F0.wireOp",EDGE,"E48"),sQuery(id+"F0.wireOp",EDGE,"E49"),sQuery(id+"F0.wireOp",EDGE,"E50"),sQuery(id+"F0.wireOp",EDGE,"E51"),sQuery(id+"F0.wireOp",EDGE,"E52"),sQuery(id+"F0.wireOp",EDGE,"E53"),sQuery(id+"F0.wireOp",EDGE,"E54"),sQuery(id+"F0.wireOp",EDGE,"E55"),sQuery(id+"F0.wireOp",EDGE,"E56")])],"isStart":false});
            var sketch = newSketch(context, id + "F40", { "sketchPlane" : qUnion([Q0])});
            skLineSegment(sketch, "E81.bottom", {"start": v(99.26, -45.52) * mm, "end": v(100.26, -45.52) * mm});
            skLineSegment(sketch, "E81.top", {"start": v(99.26, -88.52) * mm, "end": v(100.26, -88.52) * mm});
            skLineSegment(sketch, "E81.left", {"start": v(99.26, -45.52) * mm, "end": v(99.26, -88.52) * mm});
            skLineSegment(sketch, "E81.right", {"start": v(100.26, -45.52) * mm, "end": v(100.26, -88.52) * mm});
            skLineSegment(sketch, "E82.bottom", {"start": v(116.59, -45.52) * mm, "end": v(117.59, -45.52) * mm});
            skLineSegment(sketch, "E82.top", {"start": v(116.59, -88.52) * mm, "end": v(117.59, -88.52) * mm});
            skLineSegment(sketch, "E82.left", {"start": v(116.59, -45.52) * mm, "end": v(116.59, -88.52) * mm});
            skLineSegment(sketch, "E82.right", {"start": v(117.59, -45.52) * mm, "end": v(117.59, -88.52) * mm});
            skLineSegment(sketch, "E83.bottom", {"start": v(133.91, -45.52) * mm, "end": v(134.91, -45.52) * mm});
            skLineSegment(sketch, "E83.top", {"start": v(133.91, -88.52) * mm, "end": v(134.91, -88.52) * mm});
            skLineSegment(sketch, "E83.left", {"start": v(133.91, -45.52) * mm, "end": v(133.91, -88.52) * mm});
            skLineSegment(sketch, "E83.right", {"start": v(134.91, -45.52) * mm, "end": v(134.91, -88.52) * mm});
            skSolve(sketch);
        }
        {
            var Q0;
            Q0 = qSketchRegion(id + "F40", true);
            extrude(context, id + "F41", {"entities" : qUnion([Q0]), "operationType" : NewBodyOperationType.ADD, "depth" : 1 * mm});
        }
        {
            var Q0;
            Q0=makeQuery(id+"F41.opExtrude","CAP_EDGE",EDGE,{"disambiguationData":[OSD([sQuery(id+"F40.wireOp",EDGE,"E83.right")])],"isStart":true});
            var Q1;
            Q1=makeQuery(id+"F41.opExtrude","CAP_EDGE",EDGE,{"disambiguationData":[OSD([sQuery(id+"F40.wireOp",EDGE,"E82.right")])],"isStart":true});
            var Q2;
            Q2=makeQuery(id+"F41.opExtrude","CAP_EDGE",EDGE,{"disambiguationData":[OSD([sQuery(id+"F40.wireOp",EDGE,"E81.right")])],"isStart":true});
            var Q3;
            Q3=makeQuery(id+"F41.opExtrude","CAP_EDGE",EDGE,{"disambiguationData":[OSD([sQuery(id+"F40.wireOp",EDGE,"E81.left")])],"isStart":true});
            var Q4;
            Q4=makeQuery(id+"F41.opExtrude","CAP_EDGE",EDGE,{"disambiguationData":[OSD([sQuery(id+"F40.wireOp",EDGE,"E82.left")])],"isStart":true});
            var Q5;
            Q5=makeQuery(id+"F41.opExtrude","CAP_EDGE",EDGE,{"disambiguationData":[OSD([sQuery(id+"F40.wireOp",EDGE,"E83.left")])],"isStart":true});
            fillet(context, id + "F42", {"entities" : qUnion([Q0, Q1, Q2, Q3, Q4, Q5]), "radius" : 1 * mm, "tangentPropagation" : true, "allowEdgeOverflow" : false});
        }
        {
            var Q0;
            {var subQ0=sQuery(id+"F11.wireOp",EDGE,"E62.top");var subQ26=sQuery(id+"F0.wireOp",EDGE,"E30.bottom");var subQ46=sQuery(id+"F5.wireOp",EDGE,"E57.left");Q0=makeQuery(id+"F39.boolean.opBoolean","MERGE",FACE,{"derivedFrom":[makeQuery(id+"F23.boolean.opBoolean","MERGE",FACE,{"derivedFrom":[makeQuery(id+"F22.boolean.opBoolean","SPLIT",FACE,{"disambiguationData":[TD([makeQuery(id+"F1.opExtrude","SWEPT_FACE",FACE,{"disambiguationData":[OSD([subQ26])]})])],"derivedFrom":makeQuery(id+"F18.boolean.opBoolean","MERGE",FACE,{"derivedFrom":[makeQuery(id+"F6.opExtrude","SWEPT_FACE",FACE,{"disambiguationData":[OSD([subQ46])]}),makeQuery(id+"F18.opExtrude","SWEPT_FACE",FACE,{"disambiguationData":[OSD([sQuery(id+"F17.wireOp",EDGE,"E65.top")])]})]})}),makeQuery(id+"F23.opExtrude","SWEPT_FACE",FACE,{"disambiguationData":[OSD([subQ0]),TDD([makeQuery(id+"F12.boolean.opBoolean","COPY",EDGE,{"derivedFrom":makeQuery(id+"F12.opExtrude","CAP_EDGE",EDGE,{"disambiguationData":[OSD([subQ0])],"isStart":true})})])]})]}),makeQuery(id+"F39.opExtrude","SWEPT_FACE",FACE,{"disambiguationData":[OSD([sQuery(id+"F38.wireOp",EDGE,"E80.bottom")])]})]});}
            var sketch = newSketch(context, id + "F43", { "sketchPlane" : qUnion([Q0])});
            skText(sketch, "E84", { "text": "V.2", "fontName": "OpenSans-Bold.ttf"});
            const initialGuessF43  = {"E84": [-0.09886, -0.01082, 1, 0, 0.00424]};
            skSetInitialGuess(sketch, initialGuessF43);
            skSolve(sketch);
        }
        {
            var Q0;
            Q0 = qSketchRegion(id + "F43", true);
            extrude(context, id + "F44", {"entities" : qUnion([Q0]), "operationType" : NewBodyOperationType.ADD, "depth" : 1 * mm});
        }
        {
            var Q0;
            Q0=makeQuery(id+"F31.boolean.opBoolean","MERGE",FACE,{"derivedFrom":[makeQuery(id+"F28.boolean.opBoolean","MERGE",FACE,{"derivedFrom":[makeQuery(id+"F27.boolean.opBoolean","MERGE",FACE,{"derivedFrom":[makeQuery(id+"F25.boolean.opBoolean","MERGE",FACE,{"derivedFrom":[makeQuery(id+"F6.opExtrude","CAP_FACE",FACE,{"disambiguationData":[OSD([sQuery(id+"F5.wireOp",EDGE,"E57.bottom"),sQuery(id+"F5.wireOp",EDGE,"E57.top"),sQuery(id+"F5.wireOp",EDGE,"E57.left"),sQuery(id+"F5.wireOp",EDGE,"E57.right")])],"isStart":false}),makeQuery(id+"F25.opExtrude","SWEPT_FACE",FACE,{"disambiguationData":[OSD([sQuery(id+"F24.wireOp",EDGE,"E69.top")])]})]}),makeQuery(id+"F27.opExtrude","SWEPT_FACE",FACE,{"disambiguationData":[OSD([sQuery(id+"F26.wireOp",EDGE,"E70.top")])]}),makeQuery(id+"F27.opExtrude","SWEPT_FACE",FACE,{"disambiguationData":[OSD([sQuery(id+"F26.wireOp",EDGE,"E71.top")])]}),makeQuery(id+"F27.opExtrude","SWEPT_FACE",FACE,{"disambiguationData":[OSD([sQuery(id+"F26.wireOp",EDGE,"E72.top")])]}),makeQuery(id+"F27.opExtrude","SWEPT_FACE",FACE,{"disambiguationData":[OSD([sQuery(id+"F26.wireOp",EDGE,"E73.top")])]})]}),makeQuery(id+"F28.opExtrude","SWEPT_FACE",FACE,{"disambiguationData":[OSD([sQuery(id+"F26.wireOp",EDGE,"E74.top")])]}),makeQuery(id+"F28.opExtrude","SWEPT_FACE",FACE,{"disambiguationData":[OSD([sQuery(id+"F26.wireOp",EDGE,"E75.top")])]})]}),makeQuery(id+"F31.opExtrude","SWEPT_FACE",FACE,{"disambiguationData":[OSD([sQuery(id+"F29.wireOp",EDGE,"E76.top")])]}),makeQuery(id+"F31.opExtrude","SWEPT_FACE",FACE,{"disambiguationData":[OSD([sQuery(id+"F30.wireOp",EDGE,"E77.top")])]})]});
            var sketch = newSketch(context, id + "F45", { "sketchPlane" : qUnion([Q0])});
            skLineSegment(sketch, "E85", {"start": v(43.74, 85.52) * mm, "end": v(43.74, 88.52) * mm});
            skLineSegment(sketch, "E86", {"start": v(144.74, 85.52) * mm, "end": v(144.74, 88.52) * mm});
            skSolve(sketch);
        }
        {
            var Q0;
            Q0 = qSketchRegion(id + "F45", true);
            var Q1;
            {var subQ0=sQuery(id+"F45.wireOp",EDGE,"E85");Q1=makeQuery(id+"F45.imprint","IMPRINT",FACE,{"disambiguationData":[TD([[makeQuery(id+"F45.imprint","IMPRINT",EDGE,{"derivedFrom":subQ0}),-1.0]])]});}
            extrude(context, id + "F46", {"entities" : qUnion([Q0, Q1]), "operationType" : NewBodyOperationType.REMOVE, "oppositeDirection" : true, "depth" : 25 * mm});
        }
        {
            var Q0;
            {var subQ0=sQuery(id+"F0.wireOp",EDGE,"E56");var subQ1=sQuery(id+"F0.wireOp",EDGE,"E55");var subQ2=sQuery(id+"F0.wireOp",EDGE,"E39");var subQ3=sQuery(id+"F0.wireOp",EDGE,"E34");var subQ4=sQuery(id+"F0.wireOp",EDGE,"E54");var subQ5=sQuery(id+"F0.wireOp",EDGE,"E53");var subQ6=sQuery(id+"F0.wireOp",EDGE,"E40");var subQ7=sQuery(id+"F0.wireOp",EDGE,"E33");var subQ8=sQuery(id+"F0.wireOp",EDGE,"E48");var subQ9=sQuery(id+"F0.wireOp",EDGE,"E47");var subQ10=sQuery(id+"F0.wireOp",EDGE,"E28");var subQ11=sQuery(id+"F0.wireOp",EDGE,"E23");var subQ12=sQuery(id+"F0.wireOp",EDGE,"E46");var subQ13=sQuery(id+"F0.wireOp",EDGE,"E45");var subQ14=sQuery(id+"F0.wireOp",EDGE,"E29");var subQ15=sQuery(id+"F0.wireOp",EDGE,"E22");var subQ16=sQuery(id+"F0.wireOp",EDGE,"E50");var subQ17=sQuery(id+"F0.wireOp",EDGE,"E49");var subQ18=sQuery(id+"F0.wireOp",EDGE,"E18");var subQ19=sQuery(id+"F0.wireOp",EDGE,"E13");var subQ20=sQuery(id+"F0.wireOp",EDGE,"E52");var subQ21=sQuery(id+"F0.wireOp",EDGE,"E51");var subQ22=sQuery(id+"F0.wireOp",EDGE,"E19");var subQ23=sQuery(id+"F0.wireOp",EDGE,"E12");var subQ24=sQuery(id+"F0.wireOp",EDGE,"E42");var subQ25=sQuery(id+"F0.wireOp",EDGE,"E41");var subQ26=sQuery(id+"F0.wireOp",EDGE,"E8");var subQ27=sQuery(id+"F0.wireOp",EDGE,"E3");var subQ28=sQuery(id+"F0.wireOp",EDGE,"E44");var subQ29=sQuery(id+"F0.wireOp",EDGE,"E43");var subQ30=sQuery(id+"F0.wireOp",EDGE,"E9");var subQ31=sQuery(id+"F0.wireOp",EDGE,"E2");Q0=makeQuery(id+"F3.boolean.opBoolean","MERGE",FACE,{"derivedFrom":[makeQuery(id+"F1.opExtrude","CAP_FACE",FACE,{"disambiguationData":[OSD([sQuery(id+"F0.wireOp",EDGE,"E0"),sQuery(id+"F0.wireOp",EDGE,"E1"),subQ31,subQ27,subQ26,subQ30,sQuery(id+"F0.wireOp",EDGE,"E10"),sQuery(id+"F0.wireOp",EDGE,"E11"),subQ23,subQ19,subQ18,subQ22,sQuery(id+"F0.wireOp",EDGE,"E20"),sQuery(id+"F0.wireOp",EDGE,"E21"),subQ15,subQ11,subQ10,subQ14,sQuery(id+"F0.wireOp",EDGE,"E30.bottom"),sQuery(id+"F0.wireOp",EDGE,"E30.top"),sQuery(id+"F0.wireOp",EDGE,"E30.left"),sQuery(id+"F0.wireOp",EDGE,"E30.right"),sQuery(id+"F0.wireOp",EDGE,"E31"),sQuery(id+"F0.wireOp",EDGE,"E32"),subQ7,subQ3,subQ2,subQ6,subQ25,subQ24,subQ29,subQ28,subQ13,subQ12,subQ9,subQ8,subQ17,subQ16,subQ21,subQ20,subQ5,subQ4,subQ1,subQ0])],"isStart":true}),makeQuery(id+"F3.opExtrude","CAP_FACE",FACE,{"disambiguationData":[OSD([subQ31,subQ30,subQ29,subQ28])],"isStart":true}),makeQuery(id+"F3.opExtrude","CAP_FACE",FACE,{"disambiguationData":[OSD([subQ27,subQ26,subQ25,subQ24])],"isStart":true}),makeQuery(id+"F3.opExtrude","CAP_FACE",FACE,{"disambiguationData":[OSD([subQ23,subQ22,subQ21,subQ20])],"isStart":true}),makeQuery(id+"F3.opExtrude","CAP_FACE",FACE,{"disambiguationData":[OSD([subQ19,subQ18,subQ17,subQ16])],"isStart":true}),makeQuery(id+"F3.opExtrude","CAP_FACE",FACE,{"disambiguationData":[OSD([subQ15,subQ14,subQ13,subQ12])],"isStart":true}),makeQuery(id+"F3.opExtrude","CAP_FACE",FACE,{"disambiguationData":[OSD([subQ11,subQ10,subQ9,subQ8])],"isStart":true}),makeQuery(id+"F3.opExtrude","CAP_FACE",FACE,{"disambiguationData":[OSD([subQ7,subQ6,subQ5,subQ4])],"isStart":true}),makeQuery(id+"F3.opExtrude","CAP_FACE",FACE,{"disambiguationData":[OSD([subQ3,subQ2,subQ1,subQ0])],"isStart":true})]});}
            extrude(context, id + "F47", {"entities" : qUnion([Q0]), "operationType" : NewBodyOperationType.ADD, "depth" : .1 * mm});
        }
    });
